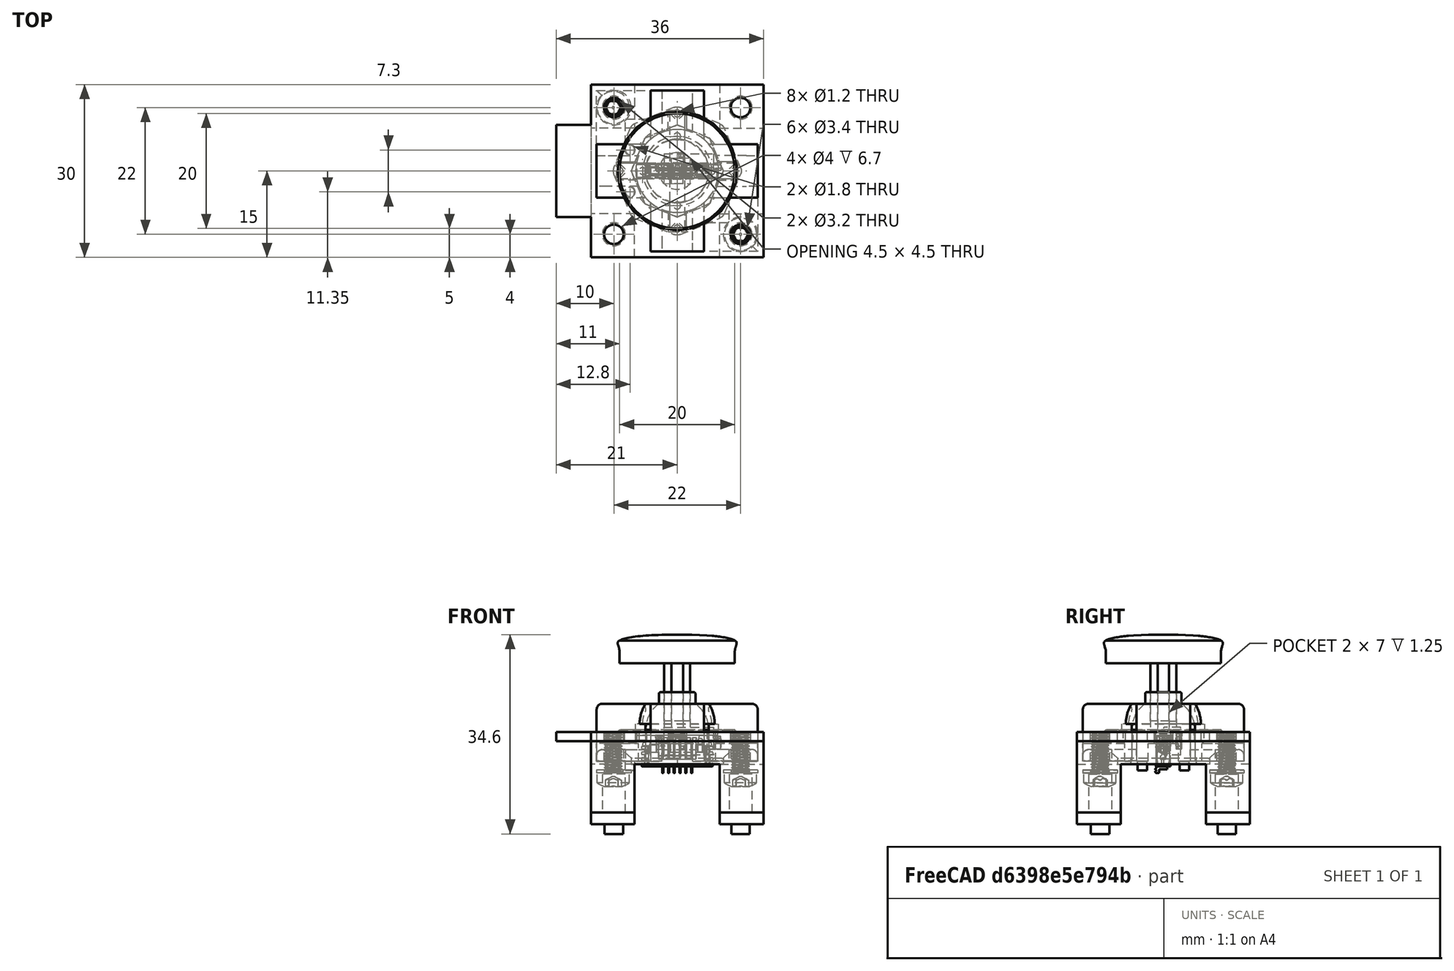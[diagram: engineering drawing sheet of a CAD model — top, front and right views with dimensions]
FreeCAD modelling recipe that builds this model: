
FCSTD DOCUMENT  (FreeCAD 0.21R33771 (Git))
Label: Thumbstick
License: All rights reserved
LicenseURL: http://en.wikipedia.org/wiki/All_rights_reserved
objects: Sketcher::SketchObject×20, PartDesign::Body×20, Part::Feature×19, PartDesign::ShapeBinder×16, App::Part×16, PartDesign::Pad×12, PartDesign::FeatureBase×11, App::DocumentObjectGroupPython×10, PartDesign::Fillet×7, PartDesign::Pocket×5, Part::FeaturePython×4, PartDesign::Revolution×3, PartDesign::Boolean×2, PartDesign::SubShapeBinder×2, Mesh::Feature×2, Spreadsheet::Sheet×1, PartDesign::Chamfer×1, App::DocumentObjectGroup×1, PartDesign::Point×1
note: 151 computed .brp shape members not serialized (recipe doc carries the construction recipe); baked Part::Feature solids carry a one-line shape summary decoded from their .brp

FEATURE [Spreadsheet::Sheet] Spreadsheet  label="params"
  cells = A2='pcb_board_outline; B2(pcb_board_outline)=30; D2='pcb_sm_brd_outline; E2(pcb_sm_brd_outline)=30; A3='pcb_mounting_distance; B3(pcb_mounting_distance)=22; D3='pcb_sm_mounting_distance; E3(pcb_sm_mounting_distance)=22; A4='pcb_sw_array_len; B4(pcb_sw_array_len)=25.11; D4='pcb_sm_array_len; E4(pcb_sm_array_len)=25.11; A6='sw_x; B6(sw_x)=11.2; D6='sw_sm_x; E6(sw_sm_x)=8.6; A7='sw_y; B7(sw_y)=4.8; D7='sw_sm_x_terms; E7(sw_sm_x_terms)=11.2; A8='sw_z; B8(sw_z)=3; D8='sw_sm_y; E8(sw_sm_y)=4.8; A9='sw_to_button_top; B9(sw_to_button_top)=3.5; D9='sw_sm_z; E9(sw_sm_z)=3; A10='sw_array_gap; B10(sw_array_gap)=4.5; D10='sw_sm_to_button_top; E10(sw_sm_to_button_top)=3.5; A11='sw_button_width; B11(sw_button_width)=2.7; D11='sw_sm_array_gap; E11(sw_sm_array_gap)=6.89; D12='sw_sm_button_width; E12(sw_sm_button_width)=2.7; A13='post_center_width; B13(post_center_width)=6; A14='post_height; B14(post_height)=8.5; A15='post_tip_height; B15(post_tip_height)=2; A16='arm_height; B16(arm_height)=2; A18='mating_cross_width; B18(mating_cross_width)=4.5; A19='mating_cross_slot_width; B19(mating_cross_slot_width)=2; A20='mating_cross_slot_depth; B20(mating_cross_slot_depth)=7; A22='swivel_shell_thickness; B22(swivel_shell_thickness)=2; A23='ccover_shell_thickness; B23(ccover_shell_thickness)=2; A25='stick_fit_tolerance; B25(stick_fit_tolerance)=0; A26='stick_extrusion_height; B26(stick_extrusion_height)=3; A27='stick_cap_height; B27(stick_cap_height)=5; A29='collar_outer_rim_height; B29(collar_outer_rim_height)=8; A30='collar_inner_rim_height; B30(collar_inner_rim_height)=7; A31='collar_width; B31(collar_width)=8; A32='collar_center_spacing; B32(collar_center_spacing)=15; A34='pcb_thickness; B34(pcb_thickness)=1.6; A35='pcb_clip_extrude; B35(pcb_clip_extrude)=1; A36='pcb_clip_overlang_length; B36(pcb_clip_overlang_length)=2.5; A38='pcb_allign_holes; B38(pcb_allign_holes)=1.6; A39='pcb_mounting_holes; B39(pcb_mounting_holes)=3; A40='pcb_sw_pth; B40(pcb_sw_pth)=1.1; A42='pcb_cover_overhang; B42(pcb_cover_overhang)=0.9; A43='pcb_clip_thickness; B43(pcb_clip_thickness)=1.5; A45='insert_length; B45(insert_length)=5.7; A46='insert_hole_dia; B46(insert_hole_dia)=4; A47='insert_min_wall_thickness; B47(insert_min_wall_thickness)=1.6
FEATURE [Sketcher::SketchObject] Sketch  label="Sketch_Arms"
  FullyConstrained = true
  MapMode = 5
  Support = -> [XY_Plane001]
  expr: Constraints[14] = <<params>>.pcb_sw_array_len - 5
  expr: Constraints[18] = <<params>>.sw_button_width
  sketch-geometry (12):
    g0: LineSegment StartX=-10.055 StartY=1.35 StartZ=0 EndX=-10.055 EndY=-1.35 EndZ=0
    g1: LineSegment StartX=-10.055 StartY=-1.35 StartZ=0 EndX=-1.35 EndY=-1.35 EndZ=0
    g2: LineSegment StartX=-1.35 StartY=-10.055 StartZ=0 EndX=1.35 EndY=-10.055 EndZ=0
    g3: LineSegment StartX=10.055 StartY=-1.35 StartZ=0 EndX=10.055 EndY=1.35 EndZ=0
    g4: LineSegment StartX=10.055 StartY=1.35 StartZ=0 EndX=1.35 EndY=1.35 EndZ=0
    g5: LineSegment StartX=1.35 StartY=1.35 StartZ=0 EndX=1.35 EndY=10.055 EndZ=0
    g6: LineSegment StartX=1.35 StartY=10.055 StartZ=0 EndX=-1.35 EndY=10.055 EndZ=0
    g7: LineSegment StartX=-1.35 StartY=10.055 StartZ=0 EndX=-1.35 EndY=1.35 EndZ=0
    g8: LineSegment StartX=-1.35 StartY=1.35 StartZ=0 EndX=-10.055 EndY=1.35 EndZ=0
    g9: LineSegment StartX=1.35 StartY=-10.055 StartZ=0 EndX=1.35 EndY=-1.35 EndZ=0
    g10: LineSegment StartX=1.35 StartY=-1.35 StartZ=0 EndX=10.055 EndY=-1.35 EndZ=0
    g11: LineSegment StartX=-1.35 StartY=-1.35 StartZ=0 EndX=-1.35 EndY=-10.055 EndZ=0
  constraints (30):
    c: Coincident(g8,g0)
    c: Coincident(g0,g1)
    c: Horizontal(g1)
    c: Coincident(g11,g2)
    c: Coincident(g2,g9)
    c: Coincident(g10,g3)
    c: Coincident(g3,g4)
    c: Coincident(g5,g6)
    c: Coincident(g6,g7)
    c: Symmetric(g11,g2,g-2)
    c: Symmetric(g6,g5,g-2)
    c: Symmetric(g8,g0,g-1)
    c: Symmetric(g3,g10,g-1)
    c: Equal(g6,g0)
    c: DistanceY(g2,g5) = 20.11
    c: Symmetric(g3,g8,g-2)
    c: Symmetric(g5,g2,g-1)
    c: Equal(g5,g4)
    c: DistanceY(g3,g3) = 2.7
    c: Horizontal(g8)
    c: Vertical(g9)
    c: Vertical(g11)
    c: Coincident(g9,g10)
    c: Coincident(g1,g11)
    c: Coincident(g8,g7)
    c: Coincident(g5,g4)
    c: Horizontal(g4)
    c: Vertical(g5)
    c: Horizontal(g10)
    c: Vertical(g7)
FEATURE [Sketcher::SketchObject] Sketch001  label="Sketch_Center"
  FullyConstrained = true
  MapMode = 5
  Placement = pos=(0,0,0) rot=(1,0,0;1.5708rad)
  Support = -> [XZ_Plane002]
  expr: Constraints[10] = <<params>>.sw_array_gap + 1
  expr: Constraints[11] = Spreadsheet.post_height
  expr: Constraints[19] = <<params>>.post_tip_height
  expr: Constraints[9] = <<params>>.arm_height
  sketch-geometry (7):
    g0: LineSegment StartX=5.5 StartY=2 StartZ=0 EndX=5.5 EndY=0 EndZ=0
    g1: LineSegment StartX=5.5 StartY=0 StartZ=0 EndX=0 EndY=0 EndZ=0
    g2: ArcOfCircle CenterX=0 CenterY=2 CenterZ=0 NormalX=0 NormalY=0 NormalZ=1 AngleXU=0 Radius=5.5 StartAngle=0 EndAngle=0.958242
    g3: LineSegment StartX=3.16228 StartY=6.5 StartZ=0 EndX=3.16228 EndY=8.5 EndZ=0
    g4: LineSegment StartX=3.16228 StartY=8.5 StartZ=0 EndX=0 EndY=8.5 EndZ=0
    g5: LineSegment StartX=0 StartY=8.5 StartZ=0 EndX=0 EndY=0 EndZ=0
    g6: LineSegment StartX=5.5 StartY=2 StartZ=0 EndX=0 EndY=2 EndZ=0
  constraints (20):
    c: PointOnObject(g0,g-1)
    c: Vertical(g0)
    c: Coincident(g1,g0)
    c: Coincident(g3,g2)
    c: Vertical(g3)
    c: Coincident(g4,g3)
    c: PointOnObject(g4,g-2)
    c: Horizontal(g4)
    c: Coincident(g5,g4)
    c: DistanceY(g0,g0) = 2
    c: DistanceX(g-1,g0) = 5.5
    c: DistanceY(g-1,g4) = 8.5
    c: Coincident(g1,g-1)
    c: Coincident(g5,g1)
    c: Coincident(g6,g0)
    c: PointOnObject(g6,g5)
    c: Horizontal(g6)
    c: Coincident(g0,g2)
    c: Coincident(g2,g6)
    c: DistanceY(g3,g3) = 2
FEATURE [PartDesign::Revolution] Revolution
  Angle = 360
  Axis = (0,-2e-16,1)
  Base = (0,0,0)
  Placement = pos=(0,0,0) rot=(1,0,0;1.5708rad)
  Profile = -> Sketch001
  ReferenceAxis = -> Sketch001 [V_Axis]
  Reversed = true
FEATURE [PartDesign::Pad] Pad  label="Pad_Arms"
  Direction = (0,0,1)
  Length = 2
  Length2 = 10
  Profile = -> Sketch
  ReferenceAxis = -> Sketch [N_Axis]
  Type = 0
  expr: Length = <<params>>.arm_height
FEATURE [PartDesign::Body] Body  label="Arms"
  Group = -> [Sketch,Pad]
  Origin = -> Origin001
  Tip = -> Pad
FEATURE [PartDesign::Boolean] Boolean
  BaseFeature = -> Revolution
  Group = -> [Body]
  Type = 0
FEATURE [PartDesign::ShapeBinder] ShapeBinder
  Placement = pos=(0,0,0) rot=(1,0,0;1.5708rad)
  Support = -> [Revolution]
  TraceSupport = false
FEATURE [Sketcher::SketchObject] Sketch002  label="Sketch_PocketMatingCross"
  FullyConstrained = true
  MapMode = 5
  Placement = pos=(0,1.9e-15,8.5) rot=(0,0,1;3.14159rad)
  Support = -> [ShapeBinder]
  expr: Constraints[32] = <<params>>.mating_cross_width
  expr: Constraints[33] = <<params>>.mating_cross_slot_width
  sketch-geometry (12):
    g0: LineSegment StartX=-2.25 StartY=1 StartZ=0 EndX=-1 EndY=1 EndZ=0
    g1: LineSegment StartX=-1 StartY=2.25 StartZ=0 EndX=-1 EndY=1 EndZ=0
    g2: LineSegment StartX=-1 StartY=2.25 StartZ=0 EndX=1 EndY=2.25 EndZ=0
    g3: LineSegment StartX=1 StartY=2.25 StartZ=0 EndX=1 EndY=1 EndZ=0
    g4: LineSegment StartX=1 StartY=1 StartZ=0 EndX=2.25 EndY=1 EndZ=0
    g5: LineSegment StartX=2.25 StartY=1 StartZ=0 EndX=2.25 EndY=-1 EndZ=0
    g6: LineSegment StartX=2.25 StartY=-1 StartZ=0 EndX=1 EndY=-1 EndZ=0
    g7: LineSegment StartX=1 StartY=-1 StartZ=0 EndX=1 EndY=-2.25 EndZ=0
    g8: LineSegment StartX=1 StartY=-2.25 StartZ=0 EndX=-1 EndY=-2.25 EndZ=0
    g9: LineSegment StartX=-1 StartY=-2.25 StartZ=0 EndX=-1 EndY=-1 EndZ=0
    g10: LineSegment StartX=-1 StartY=-1 StartZ=0 EndX=-2.25 EndY=-1 EndZ=0
    g11: LineSegment StartX=-2.25 StartY=-1 StartZ=0 EndX=-2.25 EndY=1 EndZ=0
  constraints (34):
    c: Horizontal(g0)
    c: Coincident(g1,g0)
    c: Vertical(g1)
    c: Coincident(g2,g1)
    c: Horizontal(g2)
    c: Coincident(g3,g2)
    c: Vertical(g3)
    c: Coincident(g4,g3)
    c: Horizontal(g4)
    c: Coincident(g5,g4)
    c: Vertical(g5)
    c: Coincident(g6,g5)
    c: Horizontal(g6)
    c: Coincident(g7,g6)
    c: Coincident(g8,g7)
    c: Horizontal(g8)
    c: Coincident(g9,g8)
    c: Vertical(g9)
    c: Coincident(g10,g9)
    c: Horizontal(g10)
    c: Coincident(g11,g10)
    c: Coincident(g11,g0)
    c: Vertical(g11)
    c: Equal(g11,g5)
    c: Equal(g5,g8)
    c: Equal(g8,g2)
    c: Equal(g3,g7)
    c: Equal(g4,g0)
    c: Equal(g4,g3)
    c: Symmetric(g9,g6,g-2)
    c: Symmetric(g3,g6,g-1)
    c: Vertical(g7)
    c: DistanceX(g0,g4) = 4.5
    c: DistanceX(g2,g2) = 2
FEATURE [PartDesign::Pocket] Pocket  label="Pocket_mating_cross"
  BaseFeature = -> Boolean
  Direction = (0,2e-16,-1)
  Length = 7
  Length2 = 5
  Profile = -> Sketch002
  ReferenceAxis = -> Sketch002 [N_Axis]
  Type = 0
  expr: Length = <<params>>.mating_cross_slot_depth
FEATURE [PartDesign::SubShapeBinder] Binder002  label="Binder_MatingCross_surface"
  BindCopyOnChange = 0
  BindMode = 0
  ClaimChildren = false
  Context = -> Part002 [Body003.Binder002.]
  Fuse = false
  MakeFace = true
  OffsetFill = false
  OffsetIntersection = false
  OffsetJoinType = 0
  OffsetOpenResult = false
  PartialLoad = false
  Relative = true
  Support = -> [Part[Body001.Pocket.Face45]]
  _Version = 2
FEATURE [PartDesign::Fillet] Fillet004
  Base = -> Pocket [Edge43,Edge34,Edge52,Edge59,Edge50,Edge48,Edge60,Edge56,Edge35,Edge31,Edge40,Edge44]
  BaseFeature = -> Pocket
  Radius = 1
  SupportTransform = false
  UseAllEdges = false
FEATURE [PartDesign::Fillet] Fillet005
  Base = -> Fillet004 [Edge64]
  BaseFeature = -> Fillet004
  Radius = 0.25
  SupportTransform = false
  UseAllEdges = false
FEATURE [PartDesign::Body] Body001  label="Rotation_Center_Ball"
  Group = -> [Sketch001,Revolution,Boolean,ShapeBinder,Sketch002,Pocket,Fillet004,Fillet005]
  Origin = -> Origin002
  Tip = -> Fillet005
FEATURE [App::Part] Part  label="InnerShell"
  Group = -> [Body001]
  Origin = -> Origin
FEATURE [Part::FeaturePython] Screw  label="M3x7-Screw"  # Fasteners workbench fastener (typed FeaturePython)
  Placement = pos=(11,-11,-5.5) rot=(1,0,0;3.14159rad)
  diameter = 3
  invert = false
  leftHanded = false
  length = 11
  lengthCustom = 7
  matchOuter = false
  offset = 0
  thread = true
  type = 56
FEATURE [Part::FeaturePython] Washer  label="M3-Washer"  # Fasteners workbench fastener (typed FeaturePython)
  Placement = pos=(11,-11,-5.5) rot=(0,0,1;0rad)
  diameter = 4
  invert = false
  matchOuter = false
  offset = 0
  type = 10
FEATURE [Part::FeaturePython] Screw001  label="M3x7-Screw001"  # Fasteners workbench fastener (typed FeaturePython)
  Placement = pos=(-11.1,11,-5.5) rot=(1,0,0;3.14159rad)
  diameter = 3
  invert = false
  leftHanded = false
  length = 11
  lengthCustom = 7
  matchOuter = false
  offset = 0
  thread = true
  type = 56
FEATURE [Part::FeaturePython] Washer001  label="M3-Washer001"  # Fasteners workbench fastener (typed FeaturePython)
  Placement = pos=(-11,11,-5.5) rot=(0,0,1;0rad)
  diameter = 4
  invert = false
  matchOuter = false
  offset = 0
  type = 10
FEATURE [Sketcher::SketchObject] Sketch003  label="Sketch_ShellRevolution"
  FullyConstrained = true
  MapMode = 5
  Placement = pos=(0,0,0) rot=(1,0,0;1.5708rad)
  expr: Constraints[11] = <<params>>.sw_array_gap + 1.5
  expr: Constraints[12] = <<params>>.swivel_shell_thickness
  expr: Constraints[20] = Spreadsheet.post_height
  expr: Constraints[21] = <<params>>.post_tip_height
  expr: Constraints[7] = <<params>>.arm_height + 1
  sketch-geometry (11):
    g0: ArcOfCircle CenterX=0 CenterY=3 CenterZ=0 NormalX=0 NormalY=0 NormalZ=1 AngleXU=0 Radius=6 StartAngle=0 EndAngle=0.622827
    g1: LineSegment StartX=6 StartY=3 StartZ=0 EndX=8 EndY=3 EndZ=0
    g2: ArcOfCircle CenterX=0 CenterY=3 CenterZ=0 NormalX=0 NormalY=0 NormalZ=1 AngleXU=0 Radius=8 StartAngle=0 EndAngle=0.452817
    g3: LineSegment StartX=0 StartY=0 StartZ=0 EndX=0 EndY=3 EndZ=0
    g4: LineSegment StartX=0 StartY=3 StartZ=0 EndX=6 EndY=3 EndZ=0
    g5: LineSegment StartX=0 StartY=3 StartZ=0 EndX=0 EndY=6.5 EndZ=0
    g6: LineSegment StartX=0 StartY=6.5 StartZ=0 EndX=0 EndY=8.5 EndZ=0
    g7: LineSegment StartX=0 StartY=6.5 StartZ=0 EndX=4.8734 EndY=6.5 EndZ=0
    g8: LineSegment StartX=0 StartY=3 StartZ=0 EndX=1 EndY=3 EndZ=0
    g9: ArcOfCircle CenterX=1 CenterY=3 CenterZ=0 NormalX=0 NormalY=0 NormalZ=1 AngleXU=0 Radius=5 StartAngle=0 EndAngle=0.775397
    g10: LineSegment StartX=7.19375 StartY=6.5 StartZ=0 EndX=4.57071 EndY=6.5 EndZ=0
  constraints (31):
    c: PointOnObject(g0,g-2)
    c: Coincident(g1,g0)
    c: Horizontal(g1)
    c: Coincident(g2,g0)
    c: Coincident(g2,g1)
    c: Coincident(g3,g-1)
    c: Coincident(g3,g0)
    c: DistanceY(g3,g3) = 3
    c: Coincident(g4,g0)
    c: Coincident(g4,g0)
    c: Horizontal(g4)
    c: DistanceX(g4,g4) = 6
    c: DistanceX(g1,g1) = 2
    c: Coincident(g5,g0)
    c: PointOnObject(g5,g-2)
    c: PointOnObject(g6,g-2)
    c: Coincident(g7,g6)
    c: Coincident(g7,g0)
    c: Horizontal(g7)
    c: Coincident(g5,g7)
    c: DistanceY(g3,g6) = 8.5
    c: DistanceY(g6,g6) = 2
    c: Coincident(g8,g0)
    c: PointOnObject(g8,g4)
    c: DistanceX(g8,g8) = 1
    c: Coincident(g9,g8)
    c: Coincident(g9,g0)
    c: PointOnObject(g9,g7)
    c: Coincident(g10,g2)
    c: Coincident(g10,g9)
    c: Horizontal(g10)
FEATURE [PartDesign::Revolution] Revolution001  label="Revolution_Shell"
  Angle = 360
  Axis = (0,2e-16,1)
  Base = (0,0,0)
  Placement = pos=(0,0,0) rot=(1,0,0;1.5708rad)
  Profile = -> Sketch003
  ReferenceAxis = -> Sketch003 [V_Axis]
  Reversed = true
FEATURE [PartDesign::ShapeBinder] ShapeBinder001  label="ShapeBinder_ShellBottom"
  Placement = pos=(0,0,0) rot=(1,0,0;1.5708rad)
  Support = -> [Revolution001]
  TraceSupport = true
FEATURE [PartDesign::SubShapeBinder] Binder  label="Binder_ContactTop"
  BindCopyOnChange = 0
  BindMode = 0
  ClaimChildren = false
  Context = -> Part001 [Body015.Binder.]
  Fuse = false
  MakeFace = true
  OffsetFill = false
  OffsetIntersection = false
  OffsetJoinType = 0
  OffsetOpenResult = false
  PartialLoad = false
  Relative = true
  Support = -> [Part[Body001.Pocket.Face30,Body001.Pocket.Face26,Body001.Pocket.Face29,Body001.Pocket.Face28]]
  _Version = 2
FEATURE [PartDesign::ShapeBinder] ShapeBinder017  label="ShapeBinder_ContactArm"
  Support = -> [Fillet005]
  TraceSupport = false
FEATURE [Sketcher::SketchObject] Sketch020  label="Sketch_Top"
  FullyConstrained = true
  MapMode = 5
  Support = -> [XY_Plane056]
  sketch-geometry (14):
    g0: LineSegment StartX=15 StartY=-15 StartZ=0 EndX=15 EndY=15 EndZ=0
    g1: LineSegment StartX=15 StartY=15 StartZ=0 EndX=-15 EndY=15 EndZ=0
    g2: LineSegment StartX=-15 StartY=15 StartZ=0 EndX=-15 EndY=-15 EndZ=0
    g3: LineSegment StartX=-15 StartY=-15 StartZ=0 EndX=15 EndY=-15 EndZ=0
    g4: GeomPoint X=0 Y=0 Z=0
    g5: LineSegment StartX=0 StartY=8 StartZ=0 EndX=-5.65685 EndY=5.65685 EndZ=0
    g6: LineSegment StartX=-5.65685 StartY=5.65685 StartZ=0 EndX=-8 EndY=0 EndZ=0
    g7: LineSegment StartX=-8 StartY=0 StartZ=0 EndX=-5.65685 EndY=-5.65685 EndZ=0
    g8: LineSegment StartX=-5.65685 StartY=-5.65685 StartZ=0 EndX=-9e-16 EndY=-8 EndZ=0
    g9: LineSegment StartX=-9e-16 StartY=-8 StartZ=0 EndX=5.65685 EndY=-5.65685 EndZ=0
    g10: LineSegment StartX=5.65685 StartY=-5.65685 StartZ=0 EndX=8 EndY=0 EndZ=0
    g11: LineSegment StartX=8 StartY=0 StartZ=0 EndX=5.65685 EndY=5.65685 EndZ=0
    g12: LineSegment StartX=5.65685 StartY=5.65685 StartZ=0 EndX=0 EndY=8 EndZ=0
    g13: Circle CenterX=0 CenterY=0 CenterZ=0 NormalX=0 NormalY=0 NormalZ=1 AngleXU=0 Radius=8
  constraints (32):
    c: Coincident(g0,g1)
    c: Coincident(g1,g2)
    c: Coincident(g2,g3)
    c: Coincident(g3,g0)
    c: Horizontal(g1)
    c: Horizontal(g3)
    c: Vertical(g0)
    c: Vertical(g2)
    c: Symmetric(g1,g0,g4)
    c: Coincident(g4,g-1)
    c: Coincident(g5,g6)
    c: Coincident(g6,g7)
    c: Coincident(g7,g8)
    c: Coincident(g8,g9)
    c: Coincident(g9,g10)
    c: Coincident(g10,g11)
    c: Coincident(g11,g12)
    c: Coincident(g12,g5)
    c: Equal(g5, g6-g12) x7
    c: PointOnObject(g5,g13)
    c: PointOnObject(g6,g13)
    c: PointOnObject(g7,g13)
    c: PointOnObject(g8,g13)
    c: PointOnObject(g9,g13)
    c: PointOnObject(g10,g13)
    c: PointOnObject(g11,g13)
    c: PointOnObject(g12,g13)
    c: Coincident(g13,g4)
    c: Equal(g2,g3)
    c: PointOnObject(g5,g-2)
    c: DistanceY(g4,g5) = 8
    c: DistanceY(g0,g0) = 30
FEATURE [PartDesign::Pad] Pad010  label="Pad_SocketTop"
  Direction = (0,0,1)
  Length = 4
  Length2 = 10
  Profile = -> Sketch020
  ReferenceAxis = -> Sketch020 [N_Axis]
  Reversed = true
  Type = 0
FEATURE [PartDesign::Chamfer] Chamfer
  Angle = 45
  Base = -> Pad010 [Edge35,Edge33,Edge30,Edge27,Edge24,Edge21,Edge18,Edge15]
  BaseFeature = -> Pad010
  ChamferType = 0
  FlipDirection = false
  Size = 3
  Size2 = 1
  SupportTransform = false
  UseAllEdges = false
FEATURE [PartDesign::Fillet] Fillet011
  Base = -> Chamfer [Edge10,Edge8,Edge25,Edge49,Edge52,Edge37,Edge51,Edge50]
  BaseFeature = -> Chamfer
  Radius = 2
  SupportTransform = false
  UseAllEdges = false
FEATURE [Mesh::Feature] M3_Standard001
  Placement = pos=(-11,11,-1.4) rot=(0,0,1;0rad)
FEATURE [Mesh::Feature] M3_Standard002
  Placement = pos=(11,-11,-1.4) rot=(0,0,1;0rad)
FEATURE [App::DocumentObjectGroup] Group  label="Fasteners"
  Group = -> [Screw,Washer,Screw001,Washer001,M3_Standard001,M3_Standard002]
FEATURE [PartDesign::ShapeBinder] ShapeBinder022  label="ShapeBinder_ShellTop"
  Placement = pos=(0,0,0) rot=(1,0,0;1.5708rad)
  Support = -> [Revolution001]
  TraceSupport = false
FEATURE [Sketcher::SketchObject] Sketch004  label="Sketch_ContactCovers"
  ExternalGeometry = -> [ShapeBinder022]
  FullyConstrained = true
  MapMode = 5
  Placement = pos=(0,1e-15,3) rot=(1,0,0;3.14159rad)
  Support = -> [Revolution001]
  expr: Constraints[15] = <<params>>.sw_y + <<params>>.ccover_shell_thickness * 2 + 0.5
  sketch-geometry (16):
    g0: LineSegment StartX=4.65 StartY=-5.48885 StartZ=0 EndX=4.65 EndY=-13.9889 EndZ=0
    g1: LineSegment StartX=4.65 StartY=-13.9889 StartZ=0 EndX=-4.65 EndY=-13.9889 EndZ=0
    g2: LineSegment StartX=-4.65 StartY=-13.9889 StartZ=0 EndX=-4.65 EndY=-5.48885 EndZ=0
    g3: LineSegment StartX=-5.48885 StartY=-4.65 StartZ=0 EndX=-13.9889 EndY=-4.65 EndZ=0
    g4: LineSegment StartX=-13.9889 StartY=-4.65 StartZ=0 EndX=-13.9889 EndY=4.65 EndZ=0
    g5: LineSegment StartX=-13.9889 StartY=4.65 StartZ=0 EndX=-5.48885 EndY=4.65 EndZ=0
    g6: LineSegment StartX=13.9889 StartY=-4.65 StartZ=0 EndX=13.9889 EndY=4.65 EndZ=0
    g7: LineSegment StartX=-4.65 StartY=5.48885 StartZ=0 EndX=-4.65 EndY=13.9889 EndZ=0
    g8: LineSegment StartX=-4.65 StartY=13.9889 StartZ=0 EndX=4.65 EndY=13.9889 EndZ=0
    g9: LineSegment StartX=4.65 StartY=13.9889 StartZ=0 EndX=4.65 EndY=5.48885 EndZ=0
    g10: ArcOfCircle CenterX=0 CenterY=0 CenterZ=0 NormalX=0 NormalY=0 NormalZ=1 AngleXU=0 Radius=7.19375 StartAngle=2.43874 EndAngle=3.84444
    g11: ArcOfCircle CenterX=0 CenterY=0 CenterZ=0 NormalX=0 NormalY=0 NormalZ=1 AngleXU=0 Radius=7.19375 StartAngle=0.867947 EndAngle=2.27365
    g12: ArcOfCircle CenterX=0 CenterY=0 CenterZ=0 NormalX=0 NormalY=0 NormalZ=1 AngleXU=0 Radius=7.19375 StartAngle=4.00954 EndAngle=5.41524
    g13: ArcOfCircle CenterX=0 CenterY=0 CenterZ=0 NormalX=0 NormalY=0 NormalZ=1 AngleXU=0 Radius=7.19375 StartAngle=5.58034 EndAngle=6.98604
    g14: LineSegment StartX=5.48885 StartY=4.65 StartZ=0 EndX=13.9889 EndY=4.65 EndZ=0
    g15: LineSegment StartX=5.48885 StartY=-4.65 StartZ=0 EndX=13.9889 EndY=-4.65 EndZ=0
  constraints (44):
    c: Coincident(g0,g1)
    c: Coincident(g1,g2)
    c: Vertical(g0)
    c: Vertical(g2)
    c: Coincident(g3,g4)
    c: Coincident(g4,g5)
    c: Horizontal(g3)
    c: Horizontal(g5)
    c: Coincident(g7,g8)
    c: Coincident(g8,g9)
    c: Vertical(g7)
    c: Vertical(g9)
    c: Symmetric(g4,g3,g-1)
    c: Symmetric(g8,g7,g-2)
    c: Symmetric(g0,g1,g-2)
    c: DistanceY(g4,g4) = 9.3
    c: Equal(g4,g8)
    c: Equal(g8,g6)
    c: Equal(g6,g1)
    c: PointOnObject(g5,g-3)
    c: PointOnObject(g7,g-3)
    c: PointOnObject(g2,g-3)
    c: DistanceX(g5,g5) = 8.5
    c: Coincident(g10,g-3)
    c: Coincident(g10,g5)
    c: Coincident(g10,g3)
    c: Coincident(g11,g10)
    c: Coincident(g11,g7)
    c: Coincident(g11,g9)
    c: Coincident(g12,g10)
    c: Coincident(g12,g0)
    c: Coincident(g12,g2)
    c: Equal(g5,g9)
    c: Coincident(g13,g10)
    c: PointOnObject(g13,g-3)
    c: Coincident(g14,g13)
    c: Coincident(g14,g6)
    c: Coincident(g15,g13)
    c: Coincident(g15,g6)
    c: Horizontal(g15)
    c: Horizontal(g14)
    c: Equal(g9,g15)
    c: Equal(g15,g2)
    c: Symmetric(g6,g6,g-1)
FEATURE [PartDesign::Pad] Pad001  label="Pad_ContactShell"
  BaseFeature = -> Revolution001
  Direction = (0,-3e-16,-1)
  Length = 6.5
  Length2 = 10
  Placement = pos=(0,0,0) rot=(1,0,0;1.5708rad)
  Profile = -> Sketch004
  ReferenceAxis = -> Sketch004 [N_Axis]
  Type = 0
  expr: Length = <<params>>.sw_to_button_top + <<params>>.arm_height + 1
FEATURE [PartDesign::ShapeBinder] ShapeBinder002  label="ShapeBinder_CShell_bottom"
  Support = -> [Pad001]
  TraceSupport = false
FEATURE [Sketcher::SketchObject] Sketch018  label="Sketch_SW_Housing_cut"
  ExternalGeometry = -> [ShapeBinder002]
  FullyConstrained = true
  MapMode = 5
  Placement = pos=(0,-1.9e-15,-3.5) rot=(1,0,0;3.14159rad)
  Support = -> [Pad001]
  expr: Constraints[10] = <<params>>.ccover_shell_thickness
  expr: Constraints[9] = <<params>>.ccover_shell_thickness
  sketch-geometry (16):
    g0: LineSegment StartX=-6.68786 StartY=2.65 StartZ=0 EndX=-11.9889 EndY=2.65 EndZ=0
    g1: LineSegment StartX=-11.9889 StartY=2.65 StartZ=0 EndX=-11.9889 EndY=-2.65 EndZ=0
    g2: LineSegment StartX=-11.9889 StartY=-2.65 StartZ=0 EndX=-6.68786 EndY=-2.65 EndZ=0
    g3: ArcOfCircle CenterX=0 CenterY=1e-16 CenterZ=0 NormalX=0 NormalY=0 NormalZ=1 AngleXU=0 Radius=7.19375 StartAngle=2.76433 EndAngle=3.51885
    g4: LineSegment StartX=-2.65 StartY=6.68786 StartZ=0 EndX=-2.65 EndY=11.9889 EndZ=0
    g5: LineSegment StartX=-2.65 StartY=11.9889 StartZ=0 EndX=2.65 EndY=11.9889 EndZ=0
    g6: LineSegment StartX=2.65 StartY=11.9889 StartZ=0 EndX=2.65 EndY=6.68786 EndZ=0
    g7: LineSegment StartX=6.68786 StartY=2.65 StartZ=0 EndX=11.9889 EndY=2.65 EndZ=0
    g8: LineSegment StartX=11.9889 StartY=2.65 StartZ=0 EndX=11.9889 EndY=-2.65 EndZ=0
    g9: LineSegment StartX=11.9889 StartY=-2.65 StartZ=0 EndX=6.68786 EndY=-2.65 EndZ=0
    g10: LineSegment StartX=2.65 StartY=-6.68786 StartZ=0 EndX=2.65 EndY=-11.9889 EndZ=0
    g11: LineSegment StartX=2.65 StartY=-11.9889 StartZ=0 EndX=-2.65 EndY=-11.9889 EndZ=0
    g12: LineSegment StartX=-2.65 StartY=-11.9889 StartZ=0 EndX=-2.65 EndY=-6.68786 EndZ=0
    g13: ArcOfCircle CenterX=0 CenterY=1e-16 CenterZ=0 NormalX=0 NormalY=0 NormalZ=1 AngleXU=0 Radius=7.19375 StartAngle=4.33513 EndAngle=5.08965
    g14: ArcOfCircle CenterX=0 CenterY=1e-16 CenterZ=0 NormalX=0 NormalY=0 NormalZ=1 AngleXU=0 Radius=7.19375 StartAngle=5.90592 EndAngle=6.66045
    g15: ArcOfCircle CenterX=0 CenterY=1e-16 CenterZ=0 NormalX=0 NormalY=0 NormalZ=1 AngleXU=0 Radius=7.19375 StartAngle=1.19354 EndAngle=1.94806
  constraints (44):
    c: PointOnObject(g0,g-4)
    c: Horizontal(g0)
    c: Coincident(g1,g0)
    c: Coincident(g2,g1)
    c: Horizontal(g2)
    c: Coincident(g3,g-10)
    c: Coincident(g3,g0)
    c: Coincident(g3,g2)
    c: Symmetric(g0,g1,g-1)
    c: DistanceY(g0,g-3) = 2
    c: DistanceX(g-3,g0) = 2
    c: PointOnObject(g4,g-5)
    c: Vertical(g4)
    c: Coincident(g5,g4)
    c: Coincident(g6,g5)
    c: Vertical(g6)
    c: PointOnObject(g7,g-8)
    c: Horizontal(g7)
    c: Coincident(g8,g7)
    c: Coincident(g9,g8)
    c: PointOnObject(g10,g-10)
    c: Vertical(g10)
    c: Coincident(g11,g10)
    c: Vertical(g12)
    c: Equal(g2,g12)
    c: Equal(g12,g9)
    c: Equal(g9,g6)
    c: Coincident(g11,g12)
    c: Equal(g11,g8)
    c: Symmetric(g4,g5,g-2)
    c: Symmetric(g7,g8,g-1)
    c: Symmetric(g10,g11,g-2)
    c: Coincident(g13,g3)
    c: Coincident(g13,g12)
    c: Coincident(g13,g10)
    c: Horizontal(g9)
    c: Equal(g8,g5)
    c: Equal(g11,g1)
    c: Coincident(g14,g3)
    c: Coincident(g14,g9)
    c: Coincident(g14,g7)
    c: Coincident(g15,g3)
    c: Coincident(g15,g6)
    c: Coincident(g15,g4)
FEATURE [PartDesign::Pocket] Pocket003  label="Pocket_SW_housing"
  BaseFeature = -> Pad001
  Direction = (0,4e-16,1)
  Length = 5.5
  Length2 = 5
  Placement = pos=(0,0,0) rot=(1,0,0;1.5708rad)
  Profile = -> Sketch018
  ReferenceAxis = -> Sketch018 [N_Axis]
  Type = 0
  expr: Length = <<params>>.sw_to_button_top + <<params>>.arm_height
FEATURE [PartDesign::ShapeBinder] ShapeBinder015  label="ShapeBinder_CShell_top"
  Support = -> [Pocket003]
  TraceSupport = false
FEATURE [Sketcher::SketchObject] Sketch006  label="Sketch_SW_housing_cap"
  ExternalGeometry = -> [ShapeBinder015,Pocket003]
  FullyConstrained = true
  MapMode = 5
  Placement = pos=(0,1.6e-15,3) rot=(0,0,1;3.14159rad)
  Support = -> [Pocket003]
  sketch-geometry (16):
    g0: LineSegment StartX=-13.9889 StartY=4.65 StartZ=0 EndX=-5.48885 EndY=4.65 EndZ=0
    g1: LineSegment StartX=-13.9889 StartY=-4.65 StartZ=0 EndX=-5.48885 EndY=-4.65 EndZ=0
    g2: LineSegment StartX=-4.65 StartY=13.9889 StartZ=0 EndX=-4.65 EndY=5.48885 EndZ=0
    g3: LineSegment StartX=4.65 StartY=13.9889 StartZ=0 EndX=4.65 EndY=5.48885 EndZ=0
    g4: LineSegment StartX=5.48885 StartY=4.65 StartZ=0 EndX=13.9889 EndY=4.65 EndZ=0
    g5: LineSegment StartX=13.9889 StartY=4.65 StartZ=0 EndX=13.9889 EndY=-4.65 EndZ=0
    g6: LineSegment StartX=13.9889 StartY=-4.65 StartZ=0 EndX=5.48885 EndY=-4.65 EndZ=0
    g7: LineSegment StartX=4.65 StartY=-5.48885 StartZ=0 EndX=4.65 EndY=-13.9889 EndZ=0
    g8: LineSegment StartX=4.65 StartY=-13.9889 StartZ=0 EndX=-4.65 EndY=-13.9889 EndZ=0
    g9: LineSegment StartX=-4.65 StartY=-13.9889 StartZ=0 EndX=-4.65 EndY=-5.48885 EndZ=0
    g10: ArcOfCircle CenterX=2.064e-13 CenterY=-2.049e-13 CenterZ=0 NormalX=0 NormalY=0 NormalZ=1 AngleXU=0 Radius=7.19375 StartAngle=2.43874 EndAngle=3.84444
    g11: ArcOfCircle CenterX=2.064e-13 CenterY=-2.049e-13 CenterZ=0 NormalX=0 NormalY=0 NormalZ=1 AngleXU=0 Radius=7.19375 StartAngle=0.867947 EndAngle=2.27365
    g12: ArcOfCircle CenterX=2.064e-13 CenterY=-2.049e-13 CenterZ=0 NormalX=0 NormalY=0 NormalZ=1 AngleXU=0 Radius=7.19375 StartAngle=5.58034 EndAngle=6.98604
    g13: ArcOfCircle CenterX=2.064e-13 CenterY=-2.049e-13 CenterZ=0 NormalX=0 NormalY=0 NormalZ=1 AngleXU=0 Radius=7.19375 StartAngle=4.00954 EndAngle=5.41524
    g14: LineSegment StartX=-13.9889 StartY=-4.65 StartZ=0 EndX=-13.9889 EndY=4.65 EndZ=0
    g15: LineSegment StartX=-4.65 StartY=13.9889 StartZ=0 EndX=4.65 EndY=13.9889 EndZ=0
  constraints (36):
    c: Coincident(g2,g-4)
    c: Coincident(g3,g-4)
    c: Horizontal(g4)
    c: Coincident(g5,g-6)
    c: Vertical(g5)
    c: Coincident(g6,g5)
    c: Coincident(g7,g-5)
    c: Coincident(g8,g7)
    c: Coincident(g8,g-5)
    c: Coincident(g9,g8)
    c: Coincident(g12,g10)
    c: Coincident(g12,g4)
    c: Coincident(g13,g7)
    c: Coincident(g13,g9)
    c: Coincident(g13,g11)
    c: Coincident(g10,g11)
    c: Coincident(g12,g6)
    c: Coincident(g11,g3)
    c: Coincident(g11,g2)
    c: Coincident(g10,g0)
    c: Coincident(g10,g1)
    c: Horizontal(g0)
    c: Coincident(g5,g4)
    c: Coincident(g1,g-3)
    c: Coincident(g14,g1)
    c: Coincident(g14,g0)
    c: Coincident(g-3,g0)
    c: Coincident(g15,g2)
    c: Coincident(g15,g3)
    c: Coincident(g6,g-10)
    c: Coincident(g4,g-10)
    c: Coincident(g7,g-9)
    c: Coincident(g9,g-9)
    c: Coincident(g1,g-8)
    c: Coincident(g2,g-7)
    c: Vertical(g3)
FEATURE [PartDesign::Pad] Pad002  label="Pad_SW_Housing_cap"
  BaseFeature = -> Pocket003
  Direction = (0,5e-16,1)
  Length = 3.5
  Length2 = 10
  Placement = pos=(0,0,0) rot=(1,0,0;1.5708rad)
  Profile = -> Sketch006
  ReferenceAxis = -> Sketch006 [N_Axis]
  Type = 3
  UpToFace = -> Pocket003 [Face16]
FEATURE [PartDesign::Fillet] Fillet007  label="Fillet_InnerCollar"
  Base = -> Pad002 [Edge82]
  BaseFeature = -> Pad002
  Placement = pos=(0,0,0) rot=(1,0,0;1.5708rad)
  Radius = 1
  SupportTransform = false
  UseAllEdges = false
FEATURE [PartDesign::ShapeBinder] ShapeBinder014  label="ShapeBinderShellOuter_Base"
  Support = -> [Pad002]
  TraceSupport = false
FEATURE [PartDesign::ShapeBinder] ShapeBinder016  label="ShapeBinder_AlignmentCutout"
  Support = -> [Pad002]
  TraceSupport = false
FEATURE [Sketcher::SketchObject] Sketch019  label="Sketch_ArmPockets"
  ExternalGeometry = -> [ShapeBinder016,ShapeBinder017]
  FullyConstrained = true
  MapMode = 5
  Placement = pos=(0,1.3e-15,2) rot=(1,0,0;3.14159rad)
  Support = -> [Pad002]
  sketch-geometry (32):
    g0: LineSegment StartX=-11.9889 StartY=2.65 StartZ=0 EndX=-6.68786 EndY=2.65 EndZ=0
    g1: LineSegment StartX=-11.9889 StartY=2.65 StartZ=0 EndX=-11.9889 EndY=-2.65 EndZ=0
    g2: LineSegment StartX=-2.65 StartY=6.68786 StartZ=0 EndX=-2.65 EndY=11.9889 EndZ=0
    g3: LineSegment StartX=-2.65 StartY=11.9889 StartZ=0 EndX=2.65 EndY=11.9889 EndZ=0
    g4: LineSegment StartX=2.65 StartY=11.9889 StartZ=0 EndX=2.65 EndY=6.68786 EndZ=0
    g5: LineSegment StartX=6.68786 StartY=2.65 StartZ=0 EndX=11.9889 EndY=2.65 EndZ=0
    g6: LineSegment StartX=11.9889 StartY=2.65 StartZ=0 EndX=11.9889 EndY=-2.65 EndZ=0
    g7: LineSegment StartX=11.9889 StartY=-2.65 StartZ=0 EndX=6.68786 EndY=-2.65 EndZ=0
    g8: LineSegment StartX=2.65 StartY=-11.9889 StartZ=0 EndX=-2.65 EndY=-11.9889 EndZ=0
    g9: LineSegment StartX=-2.65 StartY=-11.9889 StartZ=0 EndX=-2.65 EndY=-6.68786 EndZ=0
    g10: LineSegment StartX=2.65 StartY=-6.68786 StartZ=0 EndX=2.65 EndY=-11.9889 EndZ=0
    g11: ArcOfCircle CenterX=0 CenterY=4e-16 CenterZ=0 NormalX=0 NormalY=0 NormalZ=1 AngleXU=0 Radius=7.19375 StartAngle=4.93668 EndAngle=5.08965
    g12: ArcOfCircle CenterX=0 CenterY=4e-16 CenterZ=0 NormalX=0 NormalY=0 NormalZ=1 AngleXU=0 Radius=7.19375 StartAngle=4.33513 EndAngle=4.4881
    g13: ArcOfCircle CenterX=0 CenterY=4e-16 CenterZ=0 NormalX=0 NormalY=0 NormalZ=1 AngleXU=0 Radius=7.19375 StartAngle=0.224291 EndAngle=0.377261
    g14: ArcOfCircle CenterX=0 CenterY=4e-16 CenterZ=0 NormalX=0 NormalY=0 NormalZ=1 AngleXU=0 Radius=7.19375 StartAngle=5.90592 EndAngle=6.05889
    g15: ArcOfCircle CenterX=0 CenterY=4e-16 CenterZ=0 NormalX=0 NormalY=0 NormalZ=1 AngleXU=0 Radius=7.19375 StartAngle=1.79509 EndAngle=1.94806
    g16: ArcOfCircle CenterX=0 CenterY=4e-16 CenterZ=0 NormalX=0 NormalY=0 NormalZ=1 AngleXU=0 Radius=7.19375 StartAngle=1.19354 EndAngle=1.34651
    g17: LineSegment StartX=-11.9889 StartY=-2.65 StartZ=0 EndX=-6.68786 EndY=-2.65 EndZ=0
    g18: ArcOfCircle CenterX=0 CenterY=4e-16 CenterZ=0 NormalX=0 NormalY=0 NormalZ=1 AngleXU=0 Radius=7.19375 StartAngle=2.76433 EndAngle=2.9173
    g19: ArcOfCircle CenterX=0 CenterY=4e-16 CenterZ=0 NormalX=0 NormalY=0 NormalZ=1 AngleXU=0 Radius=7.19375 StartAngle=3.36588 EndAngle=3.51885
    g20: LineSegment StartX=-7.01356 StartY=1.6 StartZ=0 EndX=-10.555 EndY=1.6 EndZ=0
    g21: LineSegment StartX=-10.555 StartY=1.6 StartZ=0 EndX=-10.555 EndY=-1.6 EndZ=0
    g22: LineSegment StartX=-10.555 StartY=-1.6 StartZ=0 EndX=-7.01356 EndY=-1.6 EndZ=0
    g23: LineSegment StartX=-1.6 StartY=7.01356 StartZ=0 EndX=-1.6 EndY=10.555 EndZ=0
    g24: LineSegment StartX=-1.6 StartY=10.555 StartZ=0 EndX=1.6 EndY=10.555 EndZ=0
    g25: LineSegment StartX=1.6 StartY=10.555 StartZ=0 EndX=1.6 EndY=7.01356 EndZ=0
    g26: LineSegment StartX=7.01356 StartY=1.6 StartZ=0 EndX=10.555 EndY=1.6 EndZ=0
    g27: LineSegment StartX=10.555 StartY=1.6 StartZ=0 EndX=10.555 EndY=-1.6 EndZ=0
    g28: LineSegment StartX=10.555 StartY=-1.6 StartZ=0 EndX=7.01356 EndY=-1.6 EndZ=0
    g29: LineSegment StartX=-1.6 StartY=-7.01356 StartZ=0 EndX=-1.6 EndY=-10.555 EndZ=0
    g30: LineSegment StartX=-1.6 StartY=-10.555 StartZ=0 EndX=1.6 EndY=-10.555 EndZ=0
    g31: LineSegment StartX=1.6 StartY=-10.555 StartZ=0 EndX=1.6 EndY=-7.01356 EndZ=0
  constraints (81):
    c: Coincident(g3,g2)
    c: Coincident(g4,g3)
    c: Coincident(g6,g5)
    c: Coincident(g7,g6)
    c: Coincident(g9,g8)
    c: Coincident(g10,g8)
    c: Coincident(g11,g10)
    c: Coincident(g12,g9)
    c: Coincident(g13,g5)
    c: Coincident(g15,g2)
    c: Coincident(g16,g4)
    c: Coincident(g14,g7)
    c: Coincident(g0,g-4)
    c: Coincident(g-5,g1)
    c: Vertical(g1)
    c: Coincident(g17,g1)
    c: Coincident(g17,g-6)
    c: Coincident(g-13,g8)
    c: Coincident(g9,g-11)
    c: Coincident(g10,g-12)
    c: Coincident(g8,g-13)
    c: Coincident(g-17,g15)
    c: Coincident(g-17,g13)
    c: Coincident(g-17,g14)
    c: Coincident(g-17,g16)
    c: Coincident(g-17,g11)
    c: Coincident(g12,g11)
    c: Horizontal(g5)
    c: Horizontal(g7)
    c: Horizontal(g3)
    c: Vertical(g2)
    c: Vertical(g4)
    c: Vertical(g6)
    c: Coincident(g4,g-18)
    c: Coincident(g2,g-19)
    c: Equal(g2,g5)
    c: Equal(g5,g17)
    c: Coincident(g5,g-16)
    c: Coincident(g7,g-15)
    c: Coincident(g18,g11)
    c: Coincident(g18,g0)
    c: Coincident(g19,g11)
    c: Coincident(g19,g17)
    c: Equal(g1,g6)
    c: Coincident(g0,g-6)
    c: Horizontal(g20)
    c: Coincident(g21,g20)
    c: Coincident(g22,g21)
    c: Coincident(g22,g19)
    c: Horizontal(g22)
    c: Coincident(g23,g15)
    c: Vertical(g23)
    c: Coincident(g24,g23)
    c: Coincident(g25,g24)
    c: Coincident(g25,g16)
    c: Vertical(g25)
    c: Coincident(g26,g13)
    c: Horizontal(g26)
    c: Coincident(g27,g26)
    c: Coincident(g28,g27)
    c: Coincident(g28,g14)
    c: Horizontal(g28)
    c: Symmetric(g27,g26,g-1)
    c: Symmetric(g24,g23,g-2)
    c: Symmetric(g21,g20,g-1)
    c: Coincident(g29,g12)
    c: Vertical(g29)
    c: Coincident(g30,g29)
    c: Coincident(g31,g30)
    c: Coincident(g31,g11)
    c: Vertical(g31)
    c: Symmetric(g29,g30,g-2)
    c: Equal(g20,g25)
    c: Equal(g25,g28)
    c: Equal(g28,g29)
    c: Equal(g21,g24)
    c: Equal(g24,g27)
    c: Equal(g27,g30)
    c: Coincident(g20,g18)
    c: DistanceY(g-9,g20) = 0.25
    c: DistanceX(g20,g-9) = 0.5
FEATURE [PartDesign::Pad] Pad009  label="Pad_ArmPockets"
  BaseFeature = -> Fillet007
  Direction = (0,-6e-16,-1)
  Length = 2.4
  Length2 = 10
  Placement = pos=(0,0,0) rot=(1,0,0;1.5708rad)
  Profile = -> Sketch019
  ReferenceAxis = -> Sketch019 [N_Axis]
  Type = 0
FEATURE [PartDesign::ShapeBinder] ShapeBinder009  label="ShapeBinder_Pinplacement_2"
  Placement = pos=(0,0,0) rot=(1,0,0;1.5708rad)
  Support = -> [Pad009]
  TraceSupport = false
FEATURE [Sketcher::SketchObject] Sketch014  label="Sketch_AlignmentPin_2"
  ExternalGeometry = -> [ShapeBinder009]
  FullyConstrained = true
  MapMode = 5
  Placement = pos=(0,-2.6e-15,-3.5) rot=(1,0,0;3.14159rad)
  Support = -> [ShapeBinder009]
  sketch-geometry (4):
    g0: Circle CenterX=-8.19899 CenterY=-3.65 CenterZ=0 NormalX=0 NormalY=0 NormalZ=1 AngleXU=0 Radius=0.8
    g1: LineSegment StartX=-8.19899 StartY=-3.65 StartZ=0 EndX=-8.19899 EndY=-4.65 EndZ=0
    g2: LineSegment StartX=-8.19899 StartY=-3.65 StartZ=0 EndX=-8.19899 EndY=-2.65 EndZ=0
    g3: LineSegment StartX=-8.19899 StartY=-3.65 StartZ=0 EndX=-6.19899 EndY=-3.65 EndZ=0
  constraints (13):
    c: Diameter(g0) = 1.6
    c: Coincident(g0,g1)
    c: Coincident(g2,g0)
    c: Vertical(g1)
    c: Equal(g2,g1)
    c: Vertical(g2)
    c: Coincident(g3,g0)
    c: Horizontal(g3)
    c: DistanceX(g3,g3) = 2
    c: DistanceY(g2,g2) = 1
    c: PointOnObject(g3,g-3)
    c: PointOnObject(g2,g-4)
    c: PointOnObject(g1,g-5)
FEATURE [PartDesign::Pad] Pad007  label="Pad_AlignmentPin_2"
  Direction = (0,-8e-16,-1)
  Length = 1.6
  Length2 = 10
  Placement = pos=(0,0,0) rot=(1,0,0;1.5708rad)
  Profile = -> Sketch014
  ReferenceAxis = -> Sketch014 [N_Axis]
  Type = 0
  expr: Length = <<params>>.pcb_thickness
FEATURE [PartDesign::Body] Body009  label="BoardPin2"
  Group = -> [ShapeBinder009,Sketch014,Pad007]
  Origin = -> Origin023
  Tip = -> Pad007
FEATURE [PartDesign::ShapeBinder] ShapeBinder008  label="ShapeBinder_Pinplacement_1"
  Placement = pos=(0,0,0) rot=(1,0,0;1.5708rad)
  Support = -> [Pad009]
  TraceSupport = false
FEATURE [Sketcher::SketchObject] Sketch013  label="Sketch_AlignmentPin_1"
  ExternalGeometry = -> [ShapeBinder008]
  FullyConstrained = true
  MapMode = 5
  Placement = pos=(0,-2.6e-15,-3.5) rot=(1,0,0;3.14159rad)
  Support = -> [ShapeBinder008]
  sketch-geometry (4):
    g0: Circle CenterX=-8.19899 CenterY=3.65 CenterZ=0 NormalX=0 NormalY=0 NormalZ=1 AngleXU=0 Radius=0.8
    g1: LineSegment StartX=-8.19899 StartY=3.65 StartZ=0 EndX=-8.19899 EndY=2.65 EndZ=0
    g2: LineSegment StartX=-8.19899 StartY=3.65 StartZ=0 EndX=-8.19899 EndY=4.65 EndZ=0
    g3: LineSegment StartX=-8.19899 StartY=3.65 StartZ=0 EndX=-6.19899 EndY=3.65 EndZ=0
  constraints (13):
    c: Coincident(g1,g0)
    c: Vertical(g1)
    c: Coincident(g2,g0)
    c: Vertical(g2)
    c: Diameter(g0) = 1.6
    c: Coincident(g3,g0)
    c: Horizontal(g3)
    c: Equal(g2,g1)
    c: DistanceY(g2,g2) = 1
    c: DistanceX(g3,g3) = 2
    c: PointOnObject(g2,g-5)
    c: PointOnObject(g3,g-4)
    c: PointOnObject(g1,g-3)
FEATURE [PartDesign::Pad] Pad006  label="Pad_AlignmentPin_1"
  Direction = (0,-8e-16,-1)
  Length = 1.6
  Length2 = 10
  Placement = pos=(0,0,0) rot=(1,0,0;1.5708rad)
  Profile = -> Sketch013
  ReferenceAxis = -> Sketch013 [N_Axis]
  Type = 0
  expr: Length = <<params>>.pcb_thickness * 1
FEATURE [PartDesign::Fillet] Fillet  label="Fillet_PocketWiggleRoom"
  Base = -> Pad009 [Edge187,Edge133,Edge151,Edge169]
  BaseFeature = -> Pad009
  Placement = pos=(0,0,0) rot=(1,0,0;1.5708rad)
  Radius = 1
  SupportTransform = false
  UseAllEdges = false
FEATURE [PartDesign::Fillet] Fillet009  label="Fillet_Ends"
  Base = -> Fillet [Edge197,Edge199,Edge198,Edge196]
  BaseFeature = -> Fillet
  Placement = pos=(0,0,0) rot=(1,0,0;1.5708rad)
  Radius = 1
  SupportTransform = false
  UseAllEdges = false
FEATURE [PartDesign::ShapeBinder] ShapeBinder021  label="ShapeBinder_Bottom_C"
  Support = -> [Fillet009]
  TraceSupport = false
FEATURE [Sketcher::SketchObject] Sketch025  label="Sketch_SwitchEdgeCutout"
  ExternalGeometry = -> [Fillet009,ShapeBinder021]
  FullyConstrained = true
  MapMode = 5
  Placement = pos=(0,-2.3e-15,-3.5) rot=(1,0,0;3.14159rad)
  Support = -> [Fillet009]
  sketch-geometry (16):
    g0: LineSegment StartX=-2.65 StartY=-11.9889 StartZ=0 EndX=2.65 EndY=-11.9889 EndZ=0
    g1: LineSegment StartX=2.65 StartY=-11.9889 StartZ=0 EndX=2.65 EndY=-13.9889 EndZ=0
    g2: LineSegment StartX=2.65 StartY=-13.9889 StartZ=0 EndX=-2.65 EndY=-13.9889 EndZ=0
    g3: LineSegment StartX=-2.65 StartY=-13.9889 StartZ=0 EndX=-2.65 EndY=-11.9889 EndZ=0
    g4: LineSegment StartX=11.9889 StartY=-2.65 StartZ=0 EndX=13.9889 EndY=-2.65 EndZ=0
    g5: LineSegment StartX=13.9889 StartY=-2.65 StartZ=0 EndX=13.9889 EndY=2.65 EndZ=0
    g6: LineSegment StartX=13.9889 StartY=2.65 StartZ=0 EndX=11.9889 EndY=2.65 EndZ=0
    g7: LineSegment StartX=11.9889 StartY=2.65 StartZ=0 EndX=11.9889 EndY=-2.65 EndZ=0
    g8: LineSegment StartX=2.65 StartY=11.9889 StartZ=0 EndX=-2.65 EndY=11.9889 EndZ=0
    g9: LineSegment StartX=-2.65 StartY=11.9889 StartZ=0 EndX=-2.65 EndY=13.9889 EndZ=0
    g10: LineSegment StartX=-2.65 StartY=13.9889 StartZ=0 EndX=2.65 EndY=13.9889 EndZ=0
    g11: LineSegment StartX=2.65 StartY=13.9889 StartZ=0 EndX=2.65 EndY=11.9889 EndZ=0
    g12: LineSegment StartX=-13.9889 StartY=-2.65 StartZ=0 EndX=-11.9889 EndY=-2.65 EndZ=0
    g13: LineSegment StartX=-11.9889 StartY=-2.65 StartZ=0 EndX=-11.9889 EndY=2.65 EndZ=0
    g14: LineSegment StartX=-11.9889 StartY=2.65 StartZ=0 EndX=-13.9889 EndY=2.65 EndZ=0
    g15: LineSegment StartX=-13.9889 StartY=2.65 StartZ=0 EndX=-13.9889 EndY=-2.65 EndZ=0
  constraints (43):
    c: Coincident(g0,g1)
    c: Coincident(g1,g2)
    c: Coincident(g2,g3)
    c: Coincident(g3,g0)
    c: Horizontal(g0)
    c: Horizontal(g2)
    c: Vertical(g1)
    c: Coincident(g4,g5)
    c: Coincident(g5,g6)
    c: Coincident(g6,g7)
    c: Coincident(g7,g4)
    c: Horizontal(g4)
    c: Horizontal(g6)
    c: Vertical(g5)
    c: Vertical(g7)
    c: Coincident(g8,g9)
    c: Coincident(g9,g10)
    c: Coincident(g10,g11)
    c: Coincident(g11,g8)
    c: Horizontal(g8)
    c: Horizontal(g10)
    c: Vertical(g9)
    c: Coincident(g12,g13)
    c: Coincident(g13,g14)
    c: Coincident(g14,g15)
    c: Coincident(g15,g12)
    c: Horizontal(g12)
    c: Horizontal(g14)
    c: Vertical(g15)
    c: Equal(g7,g2)
    c: Equal(g2,g8)
    c: Equal(g8,g15)
    c: Vertical(g11)
    c: Coincident(g13,g-4)
    c: PointOnObject(g14,g-5)
    c: Coincident(g12,g-4)
    c: Vertical(g3)
    c: Coincident(g0,g-6)
    c: PointOnObject(g2,g-7)
    c: Symmetric(g4,g12,g-2)
    c: Symmetric(g0,g8,g-1)
    c: Equal(g14,g11)
    c: Equal(g11,g4)
FEATURE [PartDesign::Pocket] Pocket005  label="Pocket_SwitchEdgeCutout"
  BaseFeature = -> Fillet009
  Direction = (0,6e-16,1)
  Length = 3.1
  Length2 = 5
  Placement = pos=(0,0,0) rot=(1,0,0;1.5708rad)
  Profile = -> Sketch025
  ReferenceAxis = -> Sketch025 [N_Axis]
  Type = 0
FEATURE [PartDesign::Body] Body002  label="OuterShell_part"
  Group = -> [Sketch003,Revolution001,ShapeBinder001,Sketch004,Binder,Pad001,Pocket003,Sketch006,Pad002,ShapeBinder002,Sketch018,ShapeBinder015,Fillet007,ShapeBinder016,ShapeBinder017,Sketch019,Pad009,Fillet,Fillet009,ShapeBinder021,Sketch025,Pocket005,ShapeBinder022]
  Origin = -> Origin004
  Tip = -> Pocket005
FEATURE [PartDesign::Point] DatumPoint
  AttacherType = Attacher::AttachEnginePoint
  MapMode = 37
  Placement = pos=(-8.19899,-3.65,-5.1) rot=(0,0,1;0rad)
  Support = -> [Pad006]
FEATURE [PartDesign::Body] Body008  label="BoardPin1"
  Group = -> [ShapeBinder008,Sketch013,Pad006,DatumPoint]
  Origin = -> Origin022
  Tip = -> Pad006
FEATURE [Part::Feature] Part__Feature167  label="D2LS_21_20M"
  shape: bbox 11.2 x 3.8 x 4.8 mm, 66 faces, 2 solids (baked)
FEATURE [App::Part] D2LS_21_20M  label="D2LS_21_20M001"
  Group = -> [Part__Feature167]
  Origin = -> Origin059
  Placement = pos=(-10,0,1.65) rot=(1,0,0;1.5708rad)
FEATURE [Part::Feature] Part__Feature168  label="D2LS_21_20M002"
  shape: bbox 11.2 x 3.8 x 4.8 mm, 66 faces, 2 solids (baked)
FEATURE [App::Part] D2LS_21_20M001  label="D2LS_21_20M003"
  Group = -> [Part__Feature168]
  Origin = -> Origin060
  Placement = pos=(-2e-16,-10,1.65) rot=(0.57735,0.57735,0.57735;2.0944rad)
FEATURE [Part::Feature] Part__Feature169  label="C_0805_2012Metric004"
  shape: bbox 2 x 1.25 x 1.25 mm, 28 faces (baked)
FEATURE [App::Part] C_0805_2012Metric002  label="C_0805_2012Metric005"
  Group = -> [Part__Feature169]
  Origin = -> Origin061
  Placement = pos=(-6,7.9625,1.65) rot=(0,0,-1;1.5708rad)
FEATURE [Part::Feature] Part__Feature170  label="D2LS_21_20M004"
  shape: bbox 11.2 x 3.8 x 4.8 mm, 66 faces, 2 solids (baked)
FEATURE [App::Part] D2LS_21_20M002  label="D2LS_21_20M005"
  Group = -> [Part__Feature170]
  Origin = -> Origin062
  Placement = pos=(-2e-16,10,1.65) rot=(0.57735,-0.57735,-0.57735;2.0944rad)
FEATURE [Part::Feature] Part__Feature171  label="C_0805_2012Metric006"
  shape: bbox 2 x 1.25 x 1.25 mm, 28 faces (baked)
FEATURE [App::Part] C_0805_2012Metric003  label="C_0805_2012Metric007"
  Group = -> [Part__Feature171]
  Origin = -> Origin063
  Placement = pos=(6,-6.9625,1.65) rot=(0,0,1;1.5708rad)
FEATURE [Part::Feature] Part__Feature172  label="D2LS_21_20M006"
  shape: bbox 11.2 x 3.8 x 4.8 mm, 66 faces, 2 solids (baked)
FEATURE [App::Part] D2LS_21_20M003  label="D2LS_21_20M007"
  Group = -> [Part__Feature172]
  Origin = -> Origin064
  Placement = pos=(10,-2e-16,1.65) rot=(0,0.707107,0.707107;3.14159rad)
FEATURE [Part::Feature] Part__Feature173  label="SOT_23_008"
  shape: bbox 2.8 x 2.9 x 1.55 mm, 124 faces (baked)
FEATURE [App::Part] SOT_23_008  label="SOT-23-008"
  Group = -> [Part__Feature173]
  Origin = -> Origin065
  Placement = pos=(-6,8,-0.05) rot=(0.707107,0.707107,0;3.14159rad)
FEATURE [Part::Feature] Part__Feature174  label="SOT_23_009"
  shape: bbox 2.8 x 2.9 x 1.55 mm, 124 faces (baked)
FEATURE [App::Part] SOT_23_009  label="SOT-23-009"
  Group = -> [Part__Feature174]
  Origin = -> Origin066
  Placement = pos=(6,-7,-0.05) rot=(0.707107,-0.707107,0;3.14159rad)
FEATURE [Part::Feature] Part__Feature175  label="C-84953-6"
  shape: bbox 13.93 x 2.661 x 6.551 mm, 402 faces (baked)
FEATURE [App::Part] TEAmp_conn_84953_6  label="TEAmp-conn-84953-6"
  Group = -> [Part__Feature175]
  Origin = -> Origin067
  Placement = pos=(-18.75,-3e-16,-0.05) rot=(-0.57735,-0.57735,0.57735;2.0944rad)
FEATURE [Part::Feature] Part__Feature176  label="thumbpad_PCB001"
  shape: bbox 36 x 30 x 1.6 mm, 24 faces (baked)
FEATURE [PartDesign::FeatureBase] BaseFeature
  BaseFeature = -> Part__Feature176
FEATURE [PartDesign::ShapeBinder] ShapeBinder018  label="ShapeBinder_PCBSurface"
  Support = -> [BaseFeature]
  TraceSupport = false
FEATURE [Sketcher::SketchObject] Sketch021  label="Sketch_InsertBase"
  ExternalGeometry = -> [Fillet011,ShapeBinder018]
  FullyConstrained = true
  MapMode = 5
  Placement = pos=(0,0,-4) rot=(1,0,0;3.14159rad)
  Support = -> [Fillet011]
  expr: Constraints[45] = <<params>>.insert_hole_dia / 2 + <<params>>.insert_min_wall_thickness
  sketch-geometry (17):
    g0: LineSegment StartX=-15 StartY=-15 StartZ=0 EndX=-7.4 EndY=-15 EndZ=0
    g1: LineSegment StartX=-7.4 StartY=-15 StartZ=0 EndX=-7.4 EndY=-7.4 EndZ=0
    g2: LineSegment StartX=-7.4 StartY=-7.4 StartZ=0 EndX=-15 EndY=-7.4 EndZ=0
    g3: LineSegment StartX=-15 StartY=-7.4 StartZ=0 EndX=-15 EndY=-15 EndZ=0
    g4: LineSegment StartX=15 StartY=-15 StartZ=0 EndX=7.4 EndY=-15 EndZ=0
    g5: LineSegment StartX=7.4 StartY=-15 StartZ=0 EndX=7.4 EndY=-7.4 EndZ=0
    g6: LineSegment StartX=7.4 StartY=-7.4 StartZ=0 EndX=15 EndY=-7.4 EndZ=0
    g7: LineSegment StartX=15 StartY=-7.4 StartZ=0 EndX=15 EndY=-15 EndZ=0
    g8: LineSegment StartX=15 StartY=15 StartZ=0 EndX=7.4 EndY=15 EndZ=0
    g9: LineSegment StartX=7.4 StartY=15 StartZ=0 EndX=7.4 EndY=7.4 EndZ=0
    g10: LineSegment StartX=7.4 StartY=7.4 StartZ=0 EndX=15 EndY=7.4 EndZ=0
    g11: LineSegment StartX=15 StartY=7.4 StartZ=0 EndX=15 EndY=15 EndZ=0
    g12: LineSegment StartX=-15 StartY=15 StartZ=0 EndX=-7.4 EndY=15 EndZ=0
    g13: LineSegment StartX=-7.4 StartY=15 StartZ=0 EndX=-7.4 EndY=7.4 EndZ=0
    g14: LineSegment StartX=-7.4 StartY=7.4 StartZ=0 EndX=-15 EndY=7.4 EndZ=0
    g15: LineSegment StartX=-15 StartY=7.4 StartZ=0 EndX=-15 EndY=15 EndZ=0
    g16: LineSegment StartX=-11 StartY=11 StartZ=0 EndX=-7.4 EndY=11 EndZ=0
  constraints (47):
    c: Coincident(g0,g1)
    c: Coincident(g1,g2)
    c: Coincident(g2,g3)
    c: Coincident(g3,g0)
    c: Horizontal(g0)
    c: Horizontal(g2)
    c: Vertical(g1)
    c: Vertical(g3)
    c: Coincident(g0,g-6)
    c: Coincident(g4,g5)
    c: Coincident(g5,g6)
    c: Coincident(g6,g7)
    c: Coincident(g7,g4)
    c: Horizontal(g4)
    c: Horizontal(g6)
    c: Vertical(g5)
    c: Vertical(g7)
    c: Coincident(g4,g-6)
    c: Coincident(g8,g9)
    c: Coincident(g9,g10)
    c: Coincident(g10,g11)
    c: Coincident(g11,g8)
    c: Horizontal(g8)
    c: Horizontal(g10)
    c: Vertical(g9)
    c: Vertical(g11)
    c: Coincident(g8,g-5)
    c: Coincident(g12,g13)
    c: Coincident(g13,g14)
    c: Coincident(g14,g15)
    c: Coincident(g15,g12)
    c: Horizontal(g12)
    c: Horizontal(g14)
    c: Vertical(g13)
    c: Vertical(g15)
    c: Coincident(g12,g-4)
    c: Equal(g14,g13)
    c: Equal(g9,g10)
    c: Equal(g5,g6)
    c: Equal(g6,g1)
    c: Equal(g1,g2)
    c: Equal(g2,g9)
    c: Equal(g9,g13)
    c: PointOnObject(g16,g13)
    c: Horizontal(g16)
    c: DistanceX(g16,g16) = 3.6
    c: Coincident(g16,g-7)
FEATURE [PartDesign::Pad] Pad011  label="Pad_InsertBase"
  BaseFeature = -> Fillet011
  Direction = (0,0,-1)
  Length = 8.4
  Length2 = 10
  Profile = -> Sketch021
  ReferenceAxis = -> Sketch021 [N_Axis]
  Type = 0
FEATURE [Sketcher::SketchObject] Sketch022  label="Sketch_InsertHole"
  ExternalGeometry = -> [Pad011]
  FullyConstrained = true
  MapMode = 5
  Placement = pos=(0,0,-12.4) rot=(1,0,0;3.14159rad)
  Support = -> [Pad011]
  expr: Constraints[14] = <<params>>.insert_hole_dia / 2 + <<params>>.insert_min_wall_thickness
  expr: Constraints[6] = <<params>>.insert_hole_dia
  sketch-geometry (6):
    g0: Circle CenterX=-11 CenterY=11 CenterZ=0 NormalX=0 NormalY=0 NormalZ=1 AngleXU=0 Radius=2
    g1: Circle CenterX=11 CenterY=11 CenterZ=0 NormalX=0 NormalY=0 NormalZ=1 AngleXU=0 Radius=2
    g2: Circle CenterX=11 CenterY=-11 CenterZ=0 NormalX=0 NormalY=0 NormalZ=1 AngleXU=0 Radius=2
    g3: Circle CenterX=-11 CenterY=-11 CenterZ=0 NormalX=0 NormalY=0 NormalZ=1 AngleXU=0 Radius=2
    g4: LineSegment StartX=-11 StartY=11 StartZ=0 EndX=-11 EndY=7.4 EndZ=0
    g5: LineSegment StartX=-11 StartY=11 StartZ=0 EndX=-7.4 EndY=11 EndZ=0
  constraints (15):
    c: Symmetric(g0,g1,g-2)
    c: Symmetric(g0,g3,g-1)
    c: Symmetric(g2,g1,g-1)
    c: Equal(g0,g1)
    c: Equal(g1,g2)
    c: Equal(g2,g3)
    c: Diameter(g0) = 4
    c: Coincident(g4,g0)
    c: PointOnObject(g4,g-4)
    c: Vertical(g4)
    c: Coincident(g5,g0)
    c: PointOnObject(g5,g-3)
    c: Horizontal(g5)
    c: Equal(g4,g5)
    c: DistanceY(g4,g4) = 3.6
FEATURE [PartDesign::Pocket] Pocket004  label="Pocket_InsertHole"
  BaseFeature = -> Pad011
  Direction = (0,0,1)
  Length = 6.7
  Length2 = 5
  Profile = -> Sketch022
  ReferenceAxis = -> Sketch022 [N_Axis]
  Type = 0
  expr: Length = <<params>>.insert_length + 1
FEATURE [PartDesign::Body] Body028  label="SocketTop"
  Group = -> [Sketch020,Pad010,Chamfer,Fillet011,Sketch021,Pad011,Sketch022,Pocket004,ShapeBinder018]
  Origin = -> Origin056
  Tip = -> Pocket004
FEATURE [PartDesign::ShapeBinder] ShapeBinder019  label="ShapeBinder_PCBBottomFace"
  Support = -> [BaseFeature]
  TraceSupport = false
FEATURE [PartDesign::ShapeBinder] ShapeBinder020  label="ShapeBinder_SocketInsertBottom"
  Support = -> [Pocket004]
  TraceSupport = false
FEATURE [Sketcher::SketchObject] Sketch023  label="Sketch_3DPrintLegMount"
  ExternalGeometry = -> [ShapeBinder020]
  FullyConstrained = true
  MapMode = 5
  Support = -> [XY_Plane057,ShapeBinder019]
  sketch-geometry (4):
    g0: LineSegment StartX=-15 StartY=-15 StartZ=0 EndX=-7.4 EndY=-15 EndZ=0
    g1: LineSegment StartX=-7.4 StartY=-15 StartZ=0 EndX=-7.4 EndY=-7.4 EndZ=0
    g2: LineSegment StartX=-7.4 StartY=-7.4 StartZ=0 EndX=-15 EndY=-7.4 EndZ=0
    g3: LineSegment StartX=-15 StartY=-7.4 StartZ=0 EndX=-15 EndY=-15 EndZ=0
  constraints (10):
    c: Coincident(g0,g1)
    c: Coincident(g1,g2)
    c: Coincident(g2,g3)
    c: Coincident(g3,g0)
    c: Horizontal(g0)
    c: Horizontal(g2)
    c: Vertical(g1)
    c: Vertical(g3)
    c: Coincident(g0,g-3)
    c: Coincident(g-4,g1)
FEATURE [PartDesign::Pad] Pad012  label="Pad_3DPrintLegMount"
  Direction = (0,0,1)
  Length = 2
  Length2 = 10
  Profile = -> Sketch023
  ReferenceAxis = -> Sketch023 [N_Axis]
  Reversed = true
  Type = 0
FEATURE [Sketcher::SketchObject] Sketch024  label="Sketch_3DPrintPressFitPins"
  ExternalGeometry = -> [ShapeBinder019]
  FullyConstrained = true
  MapMode = 5
  Placement = pos=(0,0,-2) rot=(1,0,0;3.14159rad)
  Support = -> [Pad012]
  sketch-geometry (1):
    g0: Circle CenterX=-11 CenterY=11 CenterZ=0 NormalX=0 NormalY=0 NormalZ=1 AngleXU=0 Radius=1.6
  constraints (2):
    c: Coincident(g0,g-3)
    c: Tangent(g0,g-3)
FEATURE [PartDesign::Pad] Pad013  label="Pad_3DPrintPressFitPins"
  BaseFeature = -> Pad012
  Direction = (0,0,-1)
  Length = 1.696
  Length2 = 10
  Profile = -> Sketch024
  ReferenceAxis = -> Sketch024 [N_Axis]
  Type = 0
  expr: Length = <<params>>.pcb_thickness * 1.06
FEATURE [PartDesign::Body] Body029  label="3DPrintStand"
  Group = -> [ShapeBinder019,Sketch023,ShapeBinder020,Pad012,Sketch024,Pad013]
  Origin = -> Origin057
  Placement = pos=(0,0,-12.4) rot=(0,0,1;0rad)
  Tip = -> Pad013
FEATURE [Sketcher::SketchObject] Sketch026
  ExternalGeometry = -> [BaseFeature]
  FullyConstrained = true
  MapMode = 5
  Placement = pos=(0,0,1.6) rot=(0,0,1;0rad)
  Support = -> [BaseFeature]
  sketch-geometry (14):
    g0: Circle CenterX=-11 CenterY=11 CenterZ=0 NormalX=0 NormalY=0 NormalZ=1 AngleXU=0 Radius=1.7
    g1: Circle CenterX=-8.2 CenterY=3.65 CenterZ=0 NormalX=0 NormalY=0 NormalZ=1 AngleXU=0 Radius=0.9
    g2: Circle CenterX=-6 CenterY=0 CenterZ=0 NormalX=0 NormalY=0 NormalZ=1 AngleXU=0 Radius=0.6
    g3: Circle CenterX=-10 CenterY=0 CenterZ=0 NormalX=0 NormalY=0 NormalZ=1 AngleXU=0 Radius=0.6
    g4: Circle CenterX=-8.2 CenterY=-3.65 CenterZ=0 NormalX=0 NormalY=0 NormalZ=1 AngleXU=0 Radius=0.9
    g5: Circle CenterX=-11 CenterY=-11 CenterZ=0 NormalX=0 NormalY=0 NormalZ=1 AngleXU=0 Radius=1.7
    g6: Circle CenterX=0 CenterY=-10 CenterZ=0 NormalX=0 NormalY=0 NormalZ=1 AngleXU=0 Radius=0.6
    g7: Circle CenterX=0 CenterY=-6 CenterZ=0 NormalX=0 NormalY=0 NormalZ=1 AngleXU=0 Radius=0.6
    g8: Circle CenterX=0 CenterY=6 CenterZ=0 NormalX=0 NormalY=0 NormalZ=1 AngleXU=0 Radius=0.6
    g9: Circle CenterX=6 CenterY=0 CenterZ=0 NormalX=0 NormalY=0 NormalZ=1 AngleXU=0 Radius=0.6
    g10: Circle CenterX=10 CenterY=0 CenterZ=0 NormalX=0 NormalY=0 NormalZ=1 AngleXU=0 Radius=0.6
    g11: Circle CenterX=0 CenterY=10 CenterZ=0 NormalX=0 NormalY=0 NormalZ=1 AngleXU=0 Radius=0.6
    g12: Circle CenterX=11 CenterY=11 CenterZ=0 NormalX=0 NormalY=0 NormalZ=1 AngleXU=0 Radius=1.7
    g13: Circle CenterX=11 CenterY=-11 CenterZ=0 NormalX=0 NormalY=0 NormalZ=1 AngleXU=0 Radius=1.7
  constraints (31):
    c: Coincident(g0,g-3)
    c: Coincident(g1,g-16)
    c: Coincident(g2,g-15)
    c: Coincident(g3,g-14)
    c: Coincident(g4,g-13)
    c: Coincident(g5,g-12)
    c: Coincident(g6,g-11)
    c: Coincident(g7,g-10)
    c: Coincident(g8,g-6)
    c: Coincident(g9,g-7)
    c: Coincident(g10,g-8)
    c: Coincident(g11,g-5)
    c: Coincident(g12,g-4)
    c: Coincident(g13,g-9)
    c: Equal(g2,g3)
    c: Equal(g3,g7)
    c: Equal(g7,g6)
    c: Equal(g6,g9)
    c: Equal(g9,g10)
    c: Equal(g10,g8)
    c: Equal(g8,g11)
    c: Equal(g0,g5)
    c: Equal(g5,g13)
    c: Equal(g13,g12)
    c: Equal(g4,g1)
    c: Diameter(g-3) = 3.2
    c: Diameter(g-16) = 1.6
    c: Diameter(g-14) = 1.0922
    c: Diameter(g0) = 3.4
    c: Diameter(g1) = 1.8
    c: Diameter(g3) = 1.2
FEATURE [PartDesign::Pocket] Pocket006  label="Pocket_3DPrintMod"
  BaseFeature = -> BaseFeature
  Direction = (0,0,-1)
  Length = 6
  Length2 = 5
  Profile = -> Sketch026
  ReferenceAxis = -> Sketch026 [N_Axis]
  Type = 0
FEATURE [PartDesign::Body] Body031  label="PCB_3DPrint"
  BaseFeature = -> Part__Feature176
  Group = -> [BaseFeature,Sketch026,Pocket006]
  Origin = -> Origin069
  Tip = -> Pocket006
FEATURE [App::Part] thumbpad_002  label="thumbpad pcb_omron"
  Group = -> [D2LS_21_20M,D2LS_21_20M001,C_0805_2012Metric002,D2LS_21_20M002,C_0805_2012Metric003,D2LS_21_20M003,SOT_23_008,SOT_23_009,TEAmp_conn_84953_6,Body031,Part__Feature176]
  Origin = -> Origin068
  Placement = pos=(0,0,-5) rot=(0,0,1;0rad)
FEATURE [PartDesign::ShapeBinder] ShapeBinder023  label="ShapeBinder_PCBTopFace"
  Support = -> [Pocket006]
  TraceSupport = false
FEATURE [Sketcher::SketchObject] Sketch017  label="Sketch_MountingCollarExtrude"
  ExternalGeometry = -> [ShapeBinder014,ShapeBinder023]
  FullyConstrained = true
  MapMode = 5
  Placement = pos=(0,-1.1e-15,-3.5) rot=(1,0,0;3.14159rad)
  Support = -> [ShapeBinder014]
  sketch-geometry (7):
    g0: LineSegment StartX=-13.9889 StartY=-4.65 StartZ=0 EndX=-13.9889 EndY=-13.9889 EndZ=0
    g1: LineSegment StartX=-13.9889 StartY=-13.9889 StartZ=0 EndX=-4.65 EndY=-13.9889 EndZ=0
    g2: LineSegment StartX=-8.98885 StartY=-4.65 StartZ=0 EndX=-8.98885 EndY=-8.98885 EndZ=0
    g3: LineSegment StartX=-8.98885 StartY=-8.98885 StartZ=0 EndX=-4.65 EndY=-8.98885 EndZ=0
    g4: LineSegment StartX=-8.98885 StartY=-4.65 StartZ=0 EndX=-13.9889 EndY=-4.65 EndZ=0
    g5: LineSegment StartX=-4.65 StartY=-8.98885 StartZ=0 EndX=-4.65 EndY=-13.9889 EndZ=0
    g6: Circle CenterX=-11 CenterY=-11 CenterZ=0 NormalX=0 NormalY=0 NormalZ=1 AngleXU=0 Radius=1.7
  constraints (18):
    c: Coincident(g0,g-4)
    c: Vertical(g0)
    c: Coincident(g1,g0)
    c: Coincident(g1,g-5)
    c: Horizontal(g1)
    c: PointOnObject(g2,g-4)
    c: Vertical(g2)
    c: Coincident(g3,g2)
    c: PointOnObject(g3,g-5)
    c: Horizontal(g3)
    c: Coincident(g4,g2)
    c: Coincident(g4,g0)
    c: Coincident(g5,g3)
    c: Coincident(g5,g1)
    c: DistanceX(g4,g4) = 5
    c: Equal(g3,g2)
    c: Coincident(g6,g-6)
    c: Equal(g6,g-6)
FEATURE [PartDesign::Pad] Pad008  label="Pad_MountingColarExtrude"
  Direction = (0,-6e-16,-1)
  Length = 2
  Length2 = 10
  Profile = -> Sketch017
  ReferenceAxis = -> Sketch017 [N_Axis]
  Type = 0
FEATURE [PartDesign::Fillet] Fillet006
  Base = -> Pad008 [Edge6,Edge9]
  BaseFeature = -> Pad008
  Radius = 1
  SupportTransform = false
  UseAllEdges = false
FEATURE [PartDesign::Body] Body011  label="MountingHoleCollar"
  Group = -> [ShapeBinder014,Sketch017,Pad008,Fillet006,ShapeBinder023]
  Origin = -> Origin036
  Placement = pos=(0,0,2.05) rot=(0,0,1;0rad)
  Tip = -> Fillet006
FEATURE [PartDesign::FeatureBase] Clone
  BaseFeature = -> Body011
  Placement = pos=(0,0,2.05) rot=(0,0,1;0rad)
FEATURE [PartDesign::Body] Body032  label="MountingHoleCollar_2"
  Group = -> [Clone]
  Origin = -> Origin070
  Placement = pos=(0,0,0) rot=(0,0,1;3.14159rad)
  Tip = -> Clone
FEATURE [App::Part] Part001  label="OuterShell"
  Group = -> [Body008,Body009,Body002,Body011,Body032]
  Origin = -> Origin003
FEATURE [Part::Feature] trajectory_line
  shape: bbox 2e-07 x 2e-07 x 10 mm, 0 faces, 0 solids (baked)
FEATURE [App::DocumentObjectGroupPython] SimpleGroup008  label="EA_Nut_ConnSide"  # scripted group (container) (typed FeaturePython)
  AnimationStepTime = 0
  AnimationSteps = 20
  Distance = 10
  Group = -> [trajectory_line]
  Revolutions = 0
  dir_vectors = (1) [(0,0,-1)]
  rot_centers = (1) [(-12.9,13,-11.8)]
  rot_vectors = (1) [(0,0,-1)]
FEATURE [Part::Feature] trajectory_line001
  shape: bbox 2e-07 x 2e-07 x 8 mm, 0 faces, 0 solids (baked)
FEATURE [App::DocumentObjectGroupPython] SimpleGroup009  label="EA_Washer_ConnSide"  # scripted group (container) (typed FeaturePython)
  AnimationStepTime = 0
  AnimationSteps = 20
  Distance = 8
  Group = -> [trajectory_line001]
  Revolutions = 0
  dir_vectors = (1) [(0,0,-1)]
  rot_centers = (1) [(-13,13,-9.5)]
  rot_vectors = (1) [(0,0,-1)]
FEATURE [Part::Feature] trajectory_line002
  shape: bbox 2e-07 x 2e-07 x 10 mm, 0 faces, 0 solids (baked)
FEATURE [App::DocumentObjectGroupPython] SimpleGroup012  label="EA_Nut_Back"  # scripted group (container) (typed FeaturePython)
  AnimationStepTime = 0
  AnimationSteps = 20
  Distance = 10
  Group = -> [trajectory_line002]
  Revolutions = 0
  dir_vectors = (1) [(0,0,-1)]
  rot_centers = (1) [(12.9,-13,-11.8)]
  rot_vectors = (1) [(0,0,-1)]
FEATURE [Part::Feature] trajectory_line003
  shape: bbox 2e-07 x 2e-07 x 8 mm, 0 faces, 0 solids (baked)
FEATURE [App::DocumentObjectGroupPython] SimpleGroup013  label="EA_Wash_Back"  # scripted group (container) (typed FeaturePython)
  AnimationStepTime = 0
  AnimationSteps = 20
  Distance = 8
  Group = -> [trajectory_line003]
  Revolutions = 0
  dir_vectors = (1) [(0,0,-1)]
  rot_centers = (1) [(13,-13,-9.5)]
  rot_vectors = (1) [(0,0,-1)]
FEATURE [Part::Feature] trajectory_line004
  shape: bbox 2e-07 x 2e-07 x 38 mm, 0 faces, 0 solids (baked)
FEATURE [App::DocumentObjectGroupPython] SimpleGroup007  label="EA_Screw_ConnSide"  # scripted group (container) (typed FeaturePython)
  AnimationStepTime = 0
  AnimationSteps = 20
  Distance = 38
  Group = -> [trajectory_line004]
  Revolutions = 0
  dir_vectors = (1) [(0,0,1)]
  rot_centers = (1) [(-13,13,-4.42354)]
  rot_vectors = (1) [(0.5,0,0.866025)]
FEATURE [Part::Feature] trajectory_line005
  shape: bbox 2e-07 x 2e-07 x 38 mm, 0 faces, 0 solids (baked)
FEATURE [App::DocumentObjectGroupPython] SimpleGroup011  label="EA_Screw_Back"  # scripted group (container) (typed FeaturePython)
  AnimationStepTime = 0
  AnimationSteps = 20
  Distance = 38
  Group = -> [trajectory_line005]
  Revolutions = 0
  dir_vectors = (1) [(0,0,1)]
  rot_centers = (1) [(13,-13,-4.78629)]
  rot_vectors = (1) [(0,0,1)]
FEATURE [Part::Feature] trajectory_line006
  shape: bbox 2e-07 x 2e-07 x 20 mm, 0 faces, 0 solids (baked)
FEATURE [App::DocumentObjectGroupPython] SimpleGroup  label="EA_ShellOuter"  # scripted group (container) (typed FeaturePython)
  AnimationStepTime = 0
  AnimationSteps = 20
  Distance = 23
  Group = -> [trajectory_line006]
  Revolutions = 0
  dir_vectors = (1) [(0,8.88178e-16,1)]
  rot_centers = (1) [(-7.2422e-08,-2.02801e-12,6.5)]
  rot_vectors = (1) [(0,8.88178e-16,1)]
FEATURE [Part::Feature] trajectory_line007
  shape: bbox 2e-07 x 2e-07 x 20 mm, 0 faces, 0 solids (baked)
FEATURE [App::DocumentObjectGroupPython] SimpleGroup014  label="EA_ShellInner"  # scripted group (container) (typed FeaturePython)
  AnimationStepTime = 0
  AnimationSteps = 20
  Distance = 7
  Group = -> [trajectory_line007]
  Revolutions = 0
  dir_vectors = (1) [(0,-2.22045e-16,1)]
  rot_centers = (1) [(-9.89234e-12,-5.97184e-12,8.5)]
  rot_vectors = (1) [(0,-2.22045e-16,1)]
FEATURE [Part::Feature] trajectory_line008
  shape: bbox 2e-07 x 2e-07 x 20 mm, 0 faces, 0 solids (baked)
FEATURE [App::DocumentObjectGroupPython] SimpleGroup015  label="EA_Stick"  # scripted group (container) (typed FeaturePython)
  AnimationStepTime = 0
  AnimationSteps = 20
  Distance = 33
  Group = -> [trajectory_line008]
  Revolutions = 0
  dir_vectors = (2) [(0,0,1),(4.44116e-33,0,-1)]
  rot_centers = (1) [(8.56216e-13,4.57324e-13,13.5)]
  rot_vectors = (1) [(4.44116e-33,0,-1)]
FEATURE [App::DocumentObjectGroupPython] ExplodedAssembly  # scripted group (container) (typed FeaturePython)
  AnimationStep = 0
  CurrentTrajectory = 0
  Group = -> [SimpleGroup008,SimpleGroup009,SimpleGroup012,SimpleGroup013,SimpleGroup007,SimpleGroup011,SimpleGroup015,SimpleGroup014,SimpleGroup]
  InAnimation = false
  RemoveAllTrajectories = false
  ResetAnimation = false
FEATURE [PartDesign::FeatureBase] Clone022
  BaseFeature = -> Body028
FEATURE [PartDesign::FeatureBase] Clone025
  BaseFeature = -> Body029
  Placement = pos=(0,0,-12.4) rot=(0,0,1;0rad)
FEATURE [PartDesign::Body] Body042  label="3DPrintStand_2"
  Group = -> [Clone025]
  Origin = -> Origin082
  Placement = pos=(0,0,0) rot=(0,0,1;3.14159rad)
  Tip = -> Clone025
FEATURE [App::Part] Part006  label="KeyboardSocket"
  Group = -> [Body028,Body029,Body042]
  Origin = -> Origin055
  Placement = pos=(0,0,11) rot=(0,0,1;0rad)
FEATURE [PartDesign::FeatureBase] Clone026
  BaseFeature = -> Body029
  Placement = pos=(0,0,-12.4) rot=(0,0,1;0rad)
FEATURE [PartDesign::Body] Body043  label="Fusion_3DPrintStand"
  Group = -> [Clone026]
  Origin = -> Origin083
  Tip = -> Clone026
FEATURE [PartDesign::FeatureBase] Clone027
  BaseFeature = -> Body042
  Placement = pos=(0,0,0) rot=(0,0,1;3.14159rad)
FEATURE [PartDesign::Body] Body044  label="Fusion_3DPrintStand_2"
  Group = -> [Clone027]
  Origin = -> Origin084
  Tip = -> Clone027
FEATURE [PartDesign::Boolean] Boolean003
  BaseFeature = -> Clone022
  Group = -> [Body043,Body044]
  Type = 0
FEATURE [PartDesign::Body] Body039  label="Fusion_SocketTop"
  Group = -> [Clone022,Boolean003]
  Origin = -> Origin079
  Tip = -> Boolean003
FEATURE [App::Part] Part008  label="Fusion_Socket"
  Group = -> [Body039]
  Origin = -> Origin078
FEATURE [PartDesign::FeatureBase] Clone028
  BaseFeature = -> Body008
FEATURE [PartDesign::Body] Body045  label="F_BoardPin_1"
  Group = -> [Clone028]
  Origin = -> Origin085
  Tip = -> Clone028
FEATURE [PartDesign::FeatureBase] Clone029
  BaseFeature = -> Body009
FEATURE [PartDesign::Body] Body046  label="F_BoardPin_2"
  Group = -> [Clone029]
  Origin = -> Origin086
  Tip = -> Clone029
FEATURE [PartDesign::FeatureBase] Clone030
  BaseFeature = -> Body002
FEATURE [PartDesign::Body] Body047  label="F_OuterShell"
  Group = -> [Clone030]
  Origin = -> Origin087
  Tip = -> Clone030
FEATURE [PartDesign::FeatureBase] Clone031
  BaseFeature = -> Body011
  Placement = pos=(0,0,2.05) rot=(0,0,1;0rad)
FEATURE [PartDesign::Body] Body048  label="F_MountingCollar_1"
  Group = -> [Clone031]
  Origin = -> Origin088
  Tip = -> Clone031
FEATURE [PartDesign::FeatureBase] Clone032
  BaseFeature = -> Body032
  Placement = pos=(0,0,0) rot=(0,0,1;3.14159rad)
FEATURE [PartDesign::Body] Body049  label="F_MountingCollar_2"
  Group = -> [Clone032]
  Origin = -> Origin089
  Tip = -> Clone032
FEATURE [App::Part] Part007  label="Fusion_OuterShell"
  Group = -> [Body047,Body045,Body046,Body048,Body049]
  Origin = -> Origin071
FEATURE [App::Part] Part002  label="Stick"
  Group = -> [Body003]
  Origin = -> Origin015
FEATURE [PartDesign::Body] Body003  label="MatingCross"
  Group = -> [Sketch007,Binder002,Pad003,ShapeBinder004,Sketch008,Revolution002]
  Origin = -> Origin016
  Tip = -> Revolution002
FEATURE [Sketcher::SketchObject] Sketch007  label="Sketch_MatingCross"
  ExternalGeometry = -> [Binder002]
  FullyConstrained = true
  Placement = pos=(-1.7487e-11,-1.0449e-11,3.5) rot=(0,0,1;0rad)
  Support = -> [Body003,Binder002]
  sketch-geometry (12):
    g0: LineSegment StartX=2.25 StartY=1 StartZ=0 EndX=2.25 EndY=-1 EndZ=0
    g1: LineSegment StartX=-2.25 StartY=-1 StartZ=0 EndX=-2.25 EndY=1 EndZ=0
    g2: LineSegment StartX=-1 StartY=2.25 StartZ=0 EndX=1 EndY=2.25 EndZ=0
    g3: LineSegment StartX=1 StartY=-2.25 StartZ=0 EndX=-1 EndY=-2.25 EndZ=0
    g4: LineSegment StartX=-2.25 StartY=1 StartZ=0 EndX=-1 EndY=1 EndZ=0
    g5: LineSegment StartX=-1 StartY=1 StartZ=0 EndX=-1 EndY=2.25 EndZ=0
    g6: LineSegment StartX=-1 StartY=-1 StartZ=0 EndX=-2.25 EndY=-1 EndZ=0
    g7: LineSegment StartX=-1 StartY=-2.25 StartZ=0 EndX=-1 EndY=-1 EndZ=0
    g8: LineSegment StartX=1 StartY=-1 StartZ=0 EndX=1 EndY=-2.25 EndZ=0
    g9: LineSegment StartX=2.25 StartY=-1 StartZ=0 EndX=1 EndY=-1 EndZ=0
    g10: LineSegment StartX=1 StartY=2.25 StartZ=0 EndX=1 EndY=1 EndZ=0
    g11: LineSegment StartX=1 StartY=1 StartZ=0 EndX=2.25 EndY=1 EndZ=0
  constraints (32):
    c: Coincident(g11,g0)
    c: Coincident(g0,g9)
    c: Coincident(g6,g1)
    c: Coincident(g1,g4)
    c: Vertical(g0)
    c: Vertical(g1)
    c: Coincident(g2,g10)
    c: Coincident(g8,g3)
    c: Coincident(g3,g7)
    c: Coincident(g5,g2)
    c: Horizontal(g2)
    c: Horizontal(g3)
    c: Horizontal(g4)
    c: Vertical(g5)
    c: Horizontal(g6)
    c: Vertical(g7)
    c: Vertical(g8)
    c: Horizontal(g9)
    c: Vertical(g10)
    c: Horizontal(g11)
    c: Coincident(g6,g7)
    c: Coincident(g5,g4)
    c: Coincident(g11,g10)
    c: Coincident(g8,g9)
    c: Symmetric(g10,g4,g-2)
    c: Symmetric(g8,g6,g-2)
    c: Symmetric(g10,g8,g-1)
    c: Equal(g6,g9)
    c: Equal(g11,g10)
    c: Equal(g5,g7)
    c: Equal(g3,g1)
    c: Coincident(g1,g-4)
FEATURE [PartDesign::Pad] Pad003  label="Pad_MatingExtrusion"
  Direction = (0,0,1)
  Length = 10
  Length2 = 10
  Placement = pos=(-1.7487e-11,-1.0449e-11,3.5) rot=(0,0,1;0rad)
  Profile = -> Sketch007
  ReferenceAxis = -> Sketch007 [N_Axis]
  Type = 0
  expr: Length = <<params>>.mating_cross_slot_depth + <<params>>.stick_extrusion_height
FEATURE [PartDesign::ShapeBinder] ShapeBinder004  label="ShapeBinder_MatingExtrusion_Top"
  Placement = pos=(0,0,10) rot=(0,0,1;0rad)
  Support = -> [Pad003]
  TraceSupport = false
FEATURE [Sketcher::SketchObject] Sketch008  label="Sketch_Cap"
  AttachmentOffset = pos=(0,0,0) rot=(1,0,0;1.5708rad)
  FullyConstrained = false
  MapMode = 5
  Placement = pos=(0,0,13.5) rot=(1,0,0;1.5708rad)
  Support = -> [ShapeBinder004]
  expr: Constraints[32] = 10
  expr: Constraints[39] = <<params>>.stick_cap_height
  sketch-geometry (20):
    g0: LineSegment StartX=0 StartY=0 StartZ=0 EndX=-10 EndY=0 EndZ=0
    g1: LineSegment StartX=-10 StartY=0 StartZ=0 EndX=-10 EndY=1.96616 EndZ=0
    g2: LineSegment StartX=-10 StartY=1.96616 StartZ=0 EndX=0 EndY=1.96616 EndZ=0
    g3-g6: Circle x4 (B-spline internal-alignment scaffolding for g7; pole/knot coordinates omitted)
    g7: BSplineCurve PolesCount=4 KnotsCount=2 Degree=3 IsPeriodic=0
    g8: GeomPoint X=-10 Y=1.96616 Z=0
    g9: GeomPoint X=-10 Y=3.96616 Z=0
    g10: Circle CenterX=-10 CenterY=3.96616 CenterZ=0 NormalX=0 NormalY=0 NormalZ=1 AngleXU=0 Radius=1
    g11: Circle CenterX=-8.28547 CenterY=4.98296 CenterZ=0 NormalX=0 NormalY=0 NormalZ=1 AngleXU=0 Radius=1
    g12: Circle CenterX=0 CenterY=5 CenterZ=0 NormalX=0 NormalY=0 NormalZ=1 AngleXU=0 Radius=1
    g13: BSplineCurve PolesCount=3 KnotsCount=2 Degree=2 IsPeriodic=0
    g14: GeomPoint X=-10 Y=3.96616 Z=0
    g15: GeomPoint X=0 Y=5 Z=0
    g16: LineSegment StartX=0 StartY=1.96616 StartZ=0 EndX=0 EndY=5 EndZ=0
    g17: LineSegment StartX=-10 StartY=2.96616 StartZ=0 EndX=-10 EndY=3.96616 EndZ=0
    g18: LineSegment StartX=-10 StartY=2.96616 StartZ=0 EndX=-10 EndY=1.96616 EndZ=0
    g19: LineSegment StartX=0 StartY=1.96616 StartZ=0 EndX=0 EndY=0 EndZ=0
  constraints (40):
    c: Coincident(g0,g1)
    c: Coincident(g1,g2)
    c: Horizontal(g0)
    c: Horizontal(g2)
    c: Vertical(g1)
    c: Coincident(g0,g-1)
    c: Weight(g3) = 1
    c: Coincident(g7,g1)
    c: Equal(g3,g4)
    c: PointOnObject(g4,g3)
    c: Equal(g3,g5)
    c: PointOnObject(g5,g4)
    c: Equal(g3,g6)
    c: PointOnObject(g7,g4)
    c: InternalAlignment(g3-g6 -> g7) x4
    c: InternalAlignment(g8,g7)
    c: InternalAlignment(g9,g7)
    c: Weight(g10) = 1
    c: Coincident(g13,g7)
    c: Equal(g10,g11)
    c: Equal(g10,g12)
    c: PointOnObject(g13,g-2)
    c: InternalAlignment(g10,g13)
    c: InternalAlignment(g11,g13)
    c: InternalAlignment(g12,g13)
    c: InternalAlignment(g14,g13)
    c: InternalAlignment(g15,g13)
    c: Coincident(g16,g2)
    c: Coincident(g16,g13)
    c: DistanceX(g0,g0) = 10
    c: Vertical(g1,g4)
    c: Coincident(g17,g4)
    c: Coincident(g17,g7)
    c: Vertical(g17)
    c: Coincident(g18,g4)
    c: Coincident(g18,g1)
    c: DistanceY(g0,g13) = 5
    c: PointOnObject(g16,g-2)
    c: Coincident(g19,g16)
    c: Coincident(g19,g0)
FEATURE [PartDesign::Revolution] Revolution002  label="Revolution_Cap"
  Angle = 360
  Axis = (0,0,1)
  Base = (0,0,13.5)
  BaseFeature = -> Pad003
  Placement = pos=(-1.7487e-11,-1.0449e-11,3.5) rot=(0,0,1;0rad)
  Profile = -> Sketch008
  ReferenceAxis = -> Sketch008 [V_Axis]
